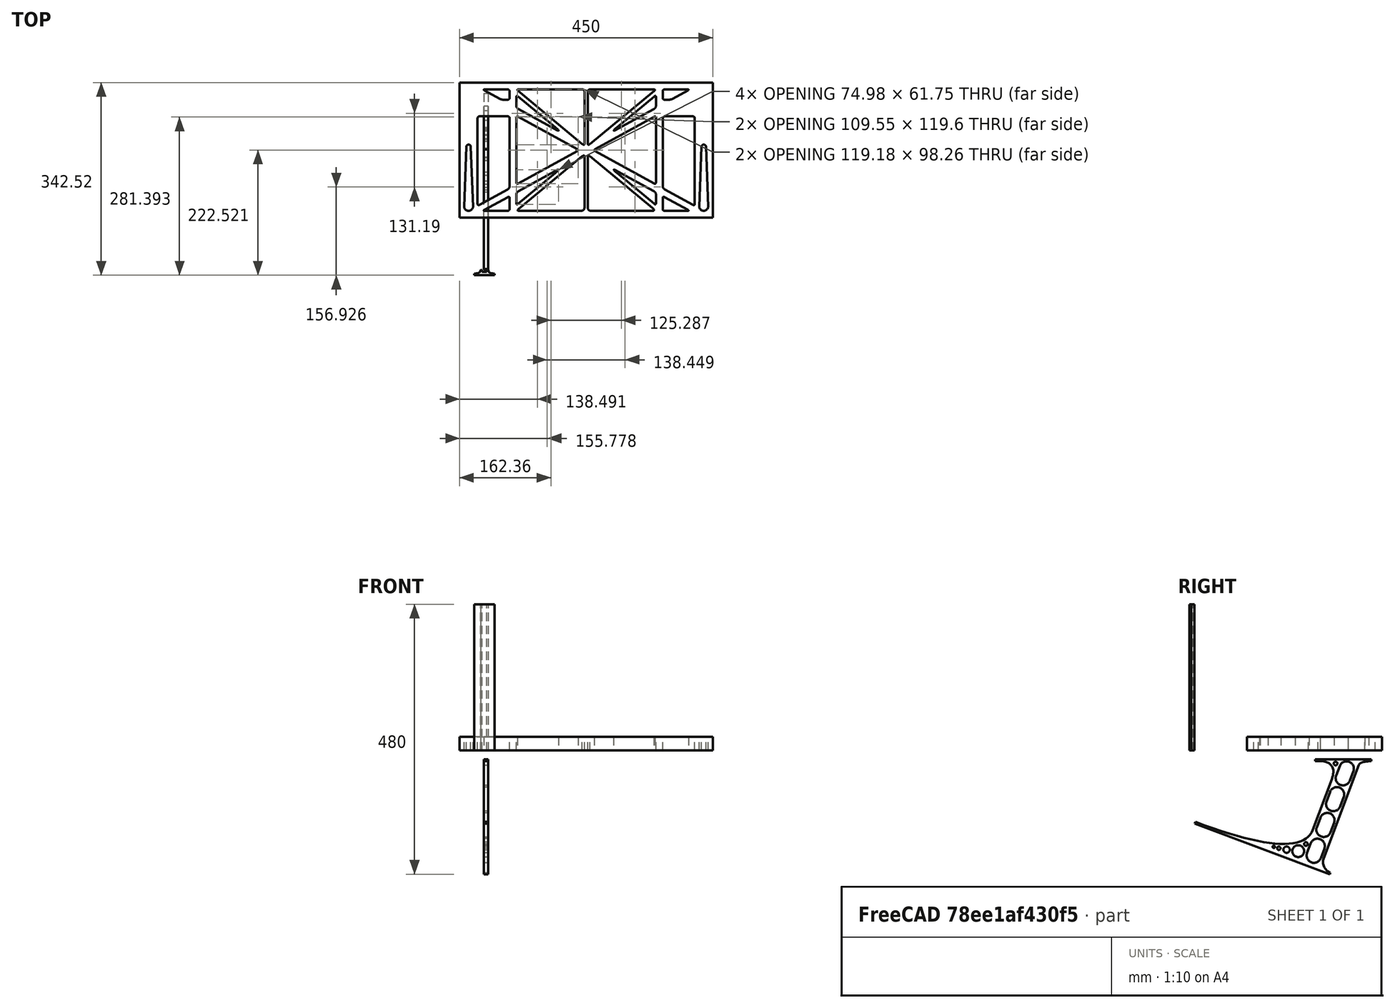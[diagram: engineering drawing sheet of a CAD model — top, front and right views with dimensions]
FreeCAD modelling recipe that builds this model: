
FCSTD DOCUMENT  (FreeCAD 0.19R0.19.2)
Label: laptopStand152FCStd
License: All rights reserved
LicenseURL: http://en.wikipedia.org/wiki/All_rights_reserved
objects: Sketcher::SketchObject×4, Part::Extrusion×3
note: 7 computed .brp shape members not serialized (recipe doc carries the construction recipe); baked Part::Feature solids carry a one-line shape summary decoded from their .brp

FEATURE [Sketcher::SketchObject] Sketch
  FullyConstrained = false
  sketch-geometry (349):
    g0: LineSegment StartX=-10.9272 StartY=-82.7794 StartZ=0 EndX=46.0728 EndY=-51.4823 EndZ=0
    g1: LineSegment StartX=-10.9272 StartY=76.4095 StartZ=0 EndX=-10.9272 EndY=-82.7794 EndZ=0
    g2: LineSegment StartX=46.0728 StartY=76.4095 StartZ=0 EndX=46.0728 EndY=-51.4823 EndZ=0
    g3: LineSegment StartX=-42.9272 StartY=136.221 StartZ=0 EndX=-42.9272 EndY=-103.779 EndZ=0
    g4: LineSegment StartX=407.073 StartY=136.221 StartZ=0 EndX=407.073 EndY=-103.779 EndZ=0
    g5: ArcOfCircle CenterX=-26.9272 CenterY=-83.7794 CenterZ=0 NormalX=0 NormalY=0 NormalZ=1 AngleXU=0 Radius=8 StartAngle=3.14159 EndAngle=6.28319
    g6: ArcOfCircle CenterX=391.073 CenterY=22.1087 CenterZ=0 NormalX=0 NormalY=0 NormalZ=1 AngleXU=0 Radius=8 StartAngle=-4.4e-15 EndAngle=3.14159
    g7: LineSegment StartX=399.073 StartY=22.1087 StartZ=0 EndX=399.073 EndY=-83.7794 EndZ=0
    g8: LineSegment StartX=383.073 StartY=22.1087 StartZ=0 EndX=383.073 EndY=-83.7794 EndZ=0
    g9: ArcOfCircle CenterX=391.073 CenterY=-83.7794 CenterZ=0 NormalX=0 NormalY=0 NormalZ=1 AngleXU=0 Radius=8 StartAngle=3.14159 EndAngle=6.28319
    g10: Circle CenterX=175.022 CenterY=27.0628 CenterZ=0 NormalX=0 NormalY=0 NormalZ=1 AngleXU=0 Radius=1
    g11: Circle CenterX=179.022 CenterY=24.8665 CenterZ=0 NormalX=0 NormalY=0 NormalZ=1 AngleXU=0 Radius=1
    g12: Circle CenterX=179.022 CenterY=27.0628 CenterZ=0 NormalX=0 NormalY=0 NormalZ=1 AngleXU=0 Radius=1
    g13: BSplineCurve PolesCount=3 KnotsCount=2 Degree=2 IsPeriodic=0
    g14: GeomPoint X=175.022 Y=27.0628 Z=0
    g15: GeomPoint X=179.022 Y=27.0628 Z=0
    g16: Circle CenterX=189.124 CenterY=27.0628 CenterZ=0 NormalX=0 NormalY=0 NormalZ=1 AngleXU=0 Radius=1
    g17: Circle CenterX=185.124 CenterY=24.8665 CenterZ=0 NormalX=0 NormalY=0 NormalZ=1 AngleXU=0 Radius=1
    g18: Circle CenterX=185.124 CenterY=27.0628 CenterZ=0 NormalX=0 NormalY=0 NormalZ=1 AngleXU=0 Radius=1
    g19: BSplineCurve PolesCount=3 KnotsCount=2 Degree=2 IsPeriodic=0
    g20: GeomPoint X=189.124 Y=27.0628 Z=0
    g21: GeomPoint X=185.124 Y=27.0628 Z=0
    g22: Circle CenterX=175.022 CenterY=5.37834 CenterZ=0 NormalX=0 NormalY=0 NormalZ=1 AngleXU=0 Radius=1
    g23: Circle CenterX=179.022 CenterY=7.57463 CenterZ=0 NormalX=0 NormalY=0 NormalZ=1 AngleXU=0 Radius=1
    g24: Circle CenterX=179.022 CenterY=5.34704 CenterZ=0 NormalX=0 NormalY=0 NormalZ=1 AngleXU=0 Radius=1
    g25: BSplineCurve PolesCount=3 KnotsCount=2 Degree=2 IsPeriodic=0
    g26: GeomPoint X=175.022 Y=5.37834 Z=0
    g27: GeomPoint X=179.022 Y=5.34704 Z=0
    g28: Circle CenterX=189.124 CenterY=5.37834 CenterZ=0 NormalX=0 NormalY=0 NormalZ=1 AngleXU=0 Radius=1
    g29: Circle CenterX=185.124 CenterY=7.57463 CenterZ=0 NormalX=0 NormalY=0 NormalZ=1 AngleXU=0 Radius=1
    g30: Circle CenterX=185.124 CenterY=5.34704 CenterZ=0 NormalX=0 NormalY=0 NormalZ=1 AngleXU=0 Radius=1
    g31: BSplineCurve PolesCount=3 KnotsCount=2 Degree=2 IsPeriodic=0
    g32: GeomPoint X=189.124 Y=5.37834 Z=0
    g33: GeomPoint X=185.124 Y=5.34704 Z=0
    g34: Circle CenterX=165.871 CenterY=18.1458 CenterZ=0 NormalX=0 NormalY=0 NormalZ=1 AngleXU=0 Radius=1
    g35: Circle CenterX=169.377 CenterY=16.2206 CenterZ=0 NormalX=0 NormalY=0 NormalZ=1 AngleXU=0 Radius=1
    g36: Circle CenterX=165.871 CenterY=14.2954 CenterZ=0 NormalX=0 NormalY=0 NormalZ=1 AngleXU=0 Radius=1
    g37: BSplineCurve PolesCount=3 KnotsCount=2 Degree=2 IsPeriodic=0
    g38: GeomPoint X=165.871 Y=18.1458 Z=0
    g39: GeomPoint X=165.871 Y=14.2954 Z=0
    g40: Circle CenterX=198.275 CenterY=18.1458 CenterZ=0 NormalX=0 NormalY=0 NormalZ=1 AngleXU=0 Radius=1
    g41: Circle CenterX=194.768 CenterY=16.2206 CenterZ=0 NormalX=0 NormalY=0 NormalZ=1 AngleXU=0 Radius=1
    g42: Circle CenterX=198.275 CenterY=14.2954 CenterZ=0 NormalX=0 NormalY=0 NormalZ=1 AngleXU=0 Radius=1
    g43: BSplineCurve PolesCount=3 KnotsCount=2 Degree=2 IsPeriodic=0
    g44: GeomPoint X=198.275 Y=18.1458 Z=0
    g45: GeomPoint X=198.275 Y=14.2954 Z=0
    g46: LineSegment StartX=407.073 StartY=-103.779 StartZ=0 EndX=-42.9272 EndY=-103.779 EndZ=0
    g47: LineSegment StartX=407.073 StartY=136.221 StartZ=0 EndX=-42.9272 EndY=136.221 EndZ=0
    g48: LineSegment StartX=46.0728 StartY=76.4095 StartZ=0 EndX=-10.9272 EndY=76.4095 EndZ=0
    g49: Circle CenterX=125.607 CenterY=54.1951 CenterZ=0 NormalX=0 NormalY=0 NormalZ=1 AngleXU=0 Radius=1
    g50: Circle CenterX=139.632 CenterY=46.4944 CenterZ=0 NormalX=0 NormalY=0 NormalZ=1 AngleXU=0 Radius=1
    g51: Circle CenterX=127.326 CenterY=56.7187 CenterZ=0 NormalX=0 NormalY=0 NormalZ=1 AngleXU=0 Radius=1
    g52: BSplineCurve PolesCount=3 KnotsCount=2 Degree=2 IsPeriodic=0
    g53: GeomPoint X=125.607 Y=54.1951 Z=0
    g54: GeomPoint X=127.326 Y=56.7187 Z=0
    g55: Circle CenterX=236.821 CenterY=56.7187 CenterZ=0 NormalX=0 NormalY=0 NormalZ=1 AngleXU=0 Radius=1
    g56: Circle CenterX=224.513 CenterY=46.4944 CenterZ=0 NormalX=0 NormalY=0 NormalZ=1 AngleXU=0 Radius=1
    g57: Circle CenterX=238.538 CenterY=54.1951 CenterZ=0 NormalX=0 NormalY=0 NormalZ=1 AngleXU=0 Radius=1
    g58: BSplineCurve PolesCount=3 KnotsCount=2 Degree=2 IsPeriodic=0
    g59: GeomPoint X=236.821 Y=56.7187 Z=0
    g60: GeomPoint X=238.538 Y=54.1951 Z=0
    g61: Circle CenterX=238.538 CenterY=-21.7539 CenterZ=0 NormalX=0 NormalY=0 NormalZ=1 AngleXU=0 Radius=1
    g62: Circle CenterX=224.513 CenterY=-14.0532 CenterZ=0 NormalX=0 NormalY=0 NormalZ=1 AngleXU=0 Radius=1
    g63: Circle CenterX=236.821 CenterY=-24.2775 CenterZ=0 NormalX=0 NormalY=0 NormalZ=1 AngleXU=0 Radius=1
    g64: BSplineCurve PolesCount=3 KnotsCount=2 Degree=2 IsPeriodic=0
    g65: GeomPoint X=238.538 Y=-21.7539 Z=0
    g66: GeomPoint X=236.821 Y=-24.2775 Z=0
    g67: Circle CenterX=125.607 CenterY=-21.7539 CenterZ=0 NormalX=0 NormalY=0 NormalZ=1 AngleXU=0 Radius=1
    g68: Circle CenterX=139.632 CenterY=-14.0532 CenterZ=0 NormalX=0 NormalY=0 NormalZ=1 AngleXU=0 Radius=1
    g69: Circle CenterX=127.325 CenterY=-24.2775 CenterZ=0 NormalX=0 NormalY=0 NormalZ=1 AngleXU=0 Radius=1
    g70: BSplineCurve PolesCount=3 KnotsCount=2 Degree=2 IsPeriodic=0
    g71: GeomPoint X=125.607 Y=-21.7539 Z=0
    g72: GeomPoint X=127.325 Y=-24.2775 Z=0
    g73: Circle CenterX=302.996 CenterY=111.695 CenterZ=0 NormalX=0 NormalY=0 NormalZ=1 AngleXU=0 Radius=1
    g74: Circle CenterX=306.073 CenterY=114.251 CenterZ=0 NormalX=0 NormalY=0 NormalZ=1 AngleXU=0 Radius=1
    g75: Circle CenterX=306.073 CenterY=110.251 CenterZ=0 NormalX=0 NormalY=0 NormalZ=1 AngleXU=0 Radius=1
    g76: BSplineCurve PolesCount=3 KnotsCount=2 Degree=2 IsPeriodic=0
    g77: GeomPoint X=302.996 Y=111.695 Z=0
    g78: GeomPoint X=306.073 Y=110.251 Z=0
    g79: Circle CenterX=306.073 CenterY=95.2763 CenterZ=0 NormalX=0 NormalY=0 NormalZ=1 AngleXU=0 Radius=1
    g80: Circle CenterX=306.073 CenterY=91.2763 CenterZ=0 NormalX=0 NormalY=0 NormalZ=1 AngleXU=0 Radius=1
    g81: Circle CenterX=302.567 CenterY=89.3511 CenterZ=0 NormalX=0 NormalY=0 NormalZ=1 AngleXU=0 Radius=1
    g82: BSplineCurve PolesCount=3 KnotsCount=2 Degree=2 IsPeriodic=0
    g83: GeomPoint X=306.073 Y=95.2763 Z=0
    g84: GeomPoint X=302.567 Y=89.3511 Z=0
    g85: LineSegment StartX=306.073 StartY=110.251 StartZ=0 EndX=306.073 EndY=95.2763 EndZ=0
    g86: LineSegment StartX=302.996 StartY=111.695 StartZ=0 EndX=236.821 EndY=56.7187 EndZ=0
    g87: LineSegment StartX=238.538 StartY=54.1951 StartZ=0 EndX=302.567 EndY=89.3511 EndZ=0
    g88: Circle CenterX=61.1496 CenterY=111.695 CenterZ=0 NormalX=0 NormalY=0 NormalZ=1 AngleXU=0 Radius=1
    g89: Circle CenterX=58.0728 CenterY=114.251 CenterZ=0 NormalX=0 NormalY=0 NormalZ=1 AngleXU=0 Radius=1
    g90: Circle CenterX=58.0728 CenterY=110.251 CenterZ=0 NormalX=0 NormalY=0 NormalZ=1 AngleXU=0 Radius=1
    g91: BSplineCurve PolesCount=3 KnotsCount=2 Degree=2 IsPeriodic=0
    g92: GeomPoint X=61.1496 Y=111.695 Z=0
    g93: GeomPoint X=58.0728 Y=110.251 Z=0
    g94: Circle CenterX=61.5791 CenterY=89.3511 CenterZ=0 NormalX=0 NormalY=0 NormalZ=1 AngleXU=0 Radius=1
    g95: Circle CenterX=58.0728 CenterY=91.2763 CenterZ=0 NormalX=0 NormalY=0 NormalZ=1 AngleXU=0 Radius=1
    g96: Circle CenterX=58.0728 CenterY=95.2763 CenterZ=0 NormalX=0 NormalY=0 NormalZ=1 AngleXU=0 Radius=1
    g97: BSplineCurve PolesCount=3 KnotsCount=2 Degree=2 IsPeriodic=0
    g98: GeomPoint X=61.5791 Y=89.3511 Z=0
    g99: GeomPoint X=58.0728 Y=95.2763 Z=0
    g100: LineSegment StartX=58.0728 StartY=110.251 StartZ=0 EndX=58.0728 EndY=95.2763 EndZ=0
    g101: LineSegment StartX=61.1496 StartY=111.695 StartZ=0 EndX=127.326 EndY=56.7187 EndZ=0
    g102: LineSegment StartX=125.607 StartY=54.1951 StartZ=0 EndX=61.5791 EndY=89.3511 EndZ=0
    g103: Circle CenterX=61.5791 CenterY=-56.9099 CenterZ=0 NormalX=0 NormalY=0 NormalZ=1 AngleXU=0 Radius=1
    g104: Circle CenterX=58.0728 CenterY=-58.8351 CenterZ=0 NormalX=0 NormalY=0 NormalZ=1 AngleXU=0 Radius=1
    g105: Circle CenterX=58.0728 CenterY=-62.8351 CenterZ=0 NormalX=0 NormalY=0 NormalZ=1 AngleXU=0 Radius=1
    g106: BSplineCurve PolesCount=3 KnotsCount=2 Degree=2 IsPeriodic=0
    g107: GeomPoint X=61.5791 Y=-56.9099 Z=0
    g108: GeomPoint X=58.0728 Y=-62.8351 Z=0
    g109: Circle CenterX=58.0728 CenterY=-77.8102 CenterZ=0 NormalX=0 NormalY=0 NormalZ=1 AngleXU=0 Radius=1
    g110: Circle CenterX=58.0728 CenterY=-81.8102 CenterZ=0 NormalX=0 NormalY=0 NormalZ=1 AngleXU=0 Radius=1
    g111: Circle CenterX=61.1496 CenterY=-79.2541 CenterZ=0 NormalX=0 NormalY=0 NormalZ=1 AngleXU=0 Radius=1
    g112: BSplineCurve PolesCount=3 KnotsCount=2 Degree=2 IsPeriodic=0
    g113: GeomPoint X=58.0728 Y=-77.8102 Z=0
    g114: GeomPoint X=61.1496 Y=-79.2541 Z=0
    g115: LineSegment StartX=58.0728 StartY=-62.8351 StartZ=0 EndX=58.0728 EndY=-77.8102 EndZ=0
    g116: LineSegment StartX=61.1496 StartY=-79.2541 StartZ=0 EndX=127.325 EndY=-24.2775 EndZ=0
    g117: LineSegment StartX=125.607 StartY=-21.7539 StartZ=0 EndX=61.5791 EndY=-56.9099 EndZ=0
    g118: Circle CenterX=302.567 CenterY=-56.9099 CenterZ=0 NormalX=0 NormalY=0 NormalZ=1 AngleXU=0 Radius=1
    g119: Circle CenterX=306.073 CenterY=-58.8351 CenterZ=0 NormalX=0 NormalY=0 NormalZ=1 AngleXU=0 Radius=1
    g120: Circle CenterX=306.073 CenterY=-62.8351 CenterZ=0 NormalX=0 NormalY=0 NormalZ=1 AngleXU=0 Radius=1
    g121: BSplineCurve PolesCount=3 KnotsCount=2 Degree=2 IsPeriodic=0
    g122: GeomPoint X=302.567 Y=-56.9099 Z=0
    g123: GeomPoint X=306.073 Y=-62.8351 Z=0
    g124: Circle CenterX=302.996 CenterY=-79.2541 CenterZ=0 NormalX=0 NormalY=0 NormalZ=1 AngleXU=0 Radius=1
    g125: Circle CenterX=306.073 CenterY=-81.8102 CenterZ=0 NormalX=0 NormalY=0 NormalZ=1 AngleXU=0 Radius=1
    g126: Circle CenterX=306.073 CenterY=-77.8102 CenterZ=0 NormalX=0 NormalY=0 NormalZ=1 AngleXU=0 Radius=1
    g127: BSplineCurve PolesCount=3 KnotsCount=2 Degree=2 IsPeriodic=0
    g128: GeomPoint X=302.996 Y=-79.2541 Z=0
    g129: GeomPoint X=306.073 Y=-77.8102 Z=0
    g130: LineSegment StartX=306.073 StartY=-62.8351 StartZ=0 EndX=306.073 EndY=-77.8102 EndZ=0
    g131: LineSegment StartX=302.996 StartY=-79.2541 StartZ=0 EndX=236.821 EndY=-24.2775 EndZ=0
    g132: LineSegment StartX=238.538 StartY=-21.7539 StartZ=0 EndX=302.567 EndY=-56.9099 EndZ=0
    g133: Circle CenterX=61.6457 CenterY=-88.8112 CenterZ=0 NormalX=0 NormalY=0 NormalZ=1 AngleXU=0 Radius=1
    g134: Circle CenterX=58.0728 CenterY=-91.7794 CenterZ=0 NormalX=0 NormalY=0 NormalZ=1 AngleXU=0 Radius=1
    g135: Circle CenterX=63.9135 CenterY=-91.7794 CenterZ=0 NormalX=0 NormalY=0 NormalZ=1 AngleXU=0 Radius=1
    g136: BSplineCurve PolesCount=3 KnotsCount=2 Degree=2 IsPeriodic=0
    g137: GeomPoint X=61.6457 Y=-88.8112 Z=0
    g138: GeomPoint X=63.9135 Y=-91.7794 Z=0
    g139: Circle CenterX=179.022 CenterY=-85.8163 CenterZ=0 NormalX=0 NormalY=0 NormalZ=1 AngleXU=0 Radius=1
    g140: Circle CenterX=179.022 CenterY=-91.7794 CenterZ=0 NormalX=0 NormalY=0 NormalZ=1 AngleXU=0 Radius=1
    g141: Circle CenterX=171.895 CenterY=-91.7794 CenterZ=0 NormalX=0 NormalY=0 NormalZ=1 AngleXU=0 Radius=1
    g142: BSplineCurve PolesCount=3 KnotsCount=2 Degree=2 IsPeriodic=0
    g143: GeomPoint X=179.022 Y=-85.8163 Z=0
    g144: GeomPoint X=171.895 Y=-91.7794 Z=0
    g145: Circle CenterX=185.124 CenterY=-86.2028 CenterZ=0 NormalX=0 NormalY=0 NormalZ=1 AngleXU=0 Radius=1
    g146: Circle CenterX=185.124 CenterY=-91.7794 CenterZ=0 NormalX=0 NormalY=0 NormalZ=1 AngleXU=0 Radius=1
    g147: Circle CenterX=191.747 CenterY=-91.7794 CenterZ=0 NormalX=0 NormalY=0 NormalZ=1 AngleXU=0 Radius=1
    g148: BSplineCurve PolesCount=3 KnotsCount=2 Degree=2 IsPeriodic=0
    g149: GeomPoint X=185.124 Y=-86.2028 Z=0
    g150: GeomPoint X=191.747 Y=-91.7794 Z=0
    g151: Circle CenterX=299.888 CenterY=-86.6413 CenterZ=0 NormalX=0 NormalY=0 NormalZ=1 AngleXU=0 Radius=1
    g152: Circle CenterX=306.073 CenterY=-91.7794 CenterZ=0 NormalX=0 NormalY=0 NormalZ=1 AngleXU=0 Radius=1
    g153: Circle CenterX=298.776 CenterY=-91.7794 CenterZ=0 NormalX=0 NormalY=0 NormalZ=1 AngleXU=0 Radius=1
    g154: BSplineCurve PolesCount=3 KnotsCount=2 Degree=2 IsPeriodic=0
    g155: GeomPoint X=299.888 Y=-86.6413 Z=0
    g156: GeomPoint X=298.776 Y=-91.7794 Z=0
    g157: LineSegment StartX=189.124 StartY=5.37834 StartZ=0 EndX=299.888 EndY=-86.6413 EndZ=0
    g158: LineSegment StartX=298.776 StartY=-91.7794 StartZ=0 EndX=191.747 EndY=-91.7794 EndZ=0
    g159: LineSegment StartX=185.124 StartY=-86.2028 StartZ=0 EndX=185.124 EndY=5.34704 EndZ=0
    g160: LineSegment StartX=179.022 StartY=5.34704 StartZ=0 EndX=179.022 EndY=-85.8163 EndZ=0
    g161: LineSegment StartX=171.895 StartY=-91.7794 StartZ=0 EndX=63.9135 EndY=-91.7794 EndZ=0
    g162: LineSegment StartX=61.6457 StartY=-88.8112 StartZ=0 EndX=175.022 EndY=5.37834 EndZ=0
    g163: Circle CenterX=302.073 CenterY=124.221 CenterZ=0 NormalX=0 NormalY=0 NormalZ=1 AngleXU=0 Radius=1
    g164: Circle CenterX=306.073 CenterY=124.221 CenterZ=0 NormalX=0 NormalY=0 NormalZ=1 AngleXU=0 Radius=1
    g165: Circle CenterX=302.996 CenterY=121.665 CenterZ=0 NormalX=0 NormalY=0 NormalZ=1 AngleXU=0 Radius=1
    g166: BSplineCurve PolesCount=3 KnotsCount=2 Degree=2 IsPeriodic=0
    g167: GeomPoint X=302.073 Y=124.221 Z=0
    g168: GeomPoint X=302.996 Y=121.665 Z=0
    g169: Circle CenterX=189.124 CenterY=124.221 CenterZ=0 NormalX=0 NormalY=0 NormalZ=1 AngleXU=0 Radius=1
    g170: Circle CenterX=185.124 CenterY=124.221 CenterZ=0 NormalX=0 NormalY=0 NormalZ=1 AngleXU=0 Radius=1
    g171: Circle CenterX=185.124 CenterY=120.221 CenterZ=0 NormalX=0 NormalY=0 NormalZ=1 AngleXU=0 Radius=1
    g172: BSplineCurve PolesCount=3 KnotsCount=2 Degree=2 IsPeriodic=0
    g173: GeomPoint X=189.124 Y=124.221 Z=0
    g174: GeomPoint X=185.124 Y=120.221 Z=0
    g175: Circle CenterX=175.022 CenterY=124.221 CenterZ=0 NormalX=0 NormalY=0 NormalZ=1 AngleXU=0 Radius=1
    g176: Circle CenterX=179.022 CenterY=124.221 CenterZ=0 NormalX=0 NormalY=0 NormalZ=1 AngleXU=0 Radius=1
    g177: Circle CenterX=179.022 CenterY=120.221 CenterZ=0 NormalX=0 NormalY=0 NormalZ=1 AngleXU=0 Radius=1
    g178: BSplineCurve PolesCount=3 KnotsCount=2 Degree=2 IsPeriodic=0
    g179: GeomPoint X=175.022 Y=124.221 Z=0
    g180: GeomPoint X=179.022 Y=120.221 Z=0
    g181: Circle CenterX=62.0728 CenterY=124.221 CenterZ=0 NormalX=0 NormalY=0 NormalZ=1 AngleXU=0 Radius=1
    g182: Circle CenterX=58.0728 CenterY=124.221 CenterZ=0 NormalX=0 NormalY=0 NormalZ=1 AngleXU=0 Radius=1
    g183: Circle CenterX=61.1496 CenterY=121.665 CenterZ=0 NormalX=0 NormalY=0 NormalZ=1 AngleXU=0 Radius=1
    g184: BSplineCurve PolesCount=3 KnotsCount=2 Degree=2 IsPeriodic=0
    g185: GeomPoint X=62.0728 Y=124.221 Z=0
    g186: GeomPoint X=61.1496 Y=121.665 Z=0
    g187: LineSegment StartX=62.0728 StartY=124.221 StartZ=0 EndX=175.022 EndY=124.221 EndZ=0
    g188: LineSegment StartX=179.022 StartY=120.221 StartZ=0 EndX=179.022 EndY=27.0628 EndZ=0
    g189: LineSegment StartX=185.124 StartY=27.0628 StartZ=0 EndX=185.124 EndY=120.221 EndZ=0
    g190: LineSegment StartX=189.124 StartY=124.221 StartZ=0 EndX=302.073 EndY=124.221 EndZ=0
    g191: LineSegment StartX=302.996 StartY=121.665 StartZ=0 EndX=189.124 EndY=27.0628 EndZ=0
    g192: LineSegment StartX=175.022 StartY=27.0628 StartZ=0 EndX=61.1496 EndY=121.665 EndZ=0
    g193: Circle CenterX=61.5791 CenterY=75.4095 CenterZ=0 NormalX=0 NormalY=0 NormalZ=1 AngleXU=0 Radius=1
    g194: Circle CenterX=58.0728 CenterY=77.3346 CenterZ=0 NormalX=0 NormalY=0 NormalZ=1 AngleXU=0 Radius=1
    g195: Circle CenterX=58.0728 CenterY=73.3346 CenterZ=0 NormalX=0 NormalY=0 NormalZ=1 AngleXU=0 Radius=1
    g196: BSplineCurve PolesCount=3 KnotsCount=2 Degree=2 IsPeriodic=0
    g197: GeomPoint X=61.5791 Y=75.4095 Z=0
    g198: GeomPoint X=58.0728 Y=73.3346 Z=0
    g199: Circle CenterX=58.0728 CenterY=-40.8935 CenterZ=0 NormalX=0 NormalY=0 NormalZ=1 AngleXU=0 Radius=1
    g200: Circle CenterX=58.0728 CenterY=-44.8935 CenterZ=0 NormalX=0 NormalY=0 NormalZ=1 AngleXU=0 Radius=1
    g201: Circle CenterX=61.5791 CenterY=-42.9683 CenterZ=0 NormalX=0 NormalY=0 NormalZ=1 AngleXU=0 Radius=1
    g202: BSplineCurve PolesCount=3 KnotsCount=2 Degree=2 IsPeriodic=0
    g203: GeomPoint X=58.0728 Y=-40.8935 Z=0
    g204: GeomPoint X=61.5791 Y=-42.9683 Z=0
    g205: LineSegment StartX=61.5791 StartY=-42.9683 StartZ=0 EndX=165.871 EndY=14.2954 EndZ=0
    g206: LineSegment StartX=165.871 StartY=18.1458 StartZ=0 EndX=61.5791 EndY=75.4095 EndZ=0
    g207: LineSegment StartX=58.0728 StartY=73.3346 StartZ=0 EndX=58.0728 EndY=-40.8935 EndZ=0
    g208: Circle CenterX=302.567 CenterY=-42.9683 CenterZ=0 NormalX=0 NormalY=0 NormalZ=1 AngleXU=0 Radius=1
    g209: Circle CenterX=306.073 CenterY=-44.8935 CenterZ=0 NormalX=0 NormalY=0 NormalZ=1 AngleXU=0 Radius=1
    g210: Circle CenterX=306.073 CenterY=-40.8935 CenterZ=0 NormalX=0 NormalY=0 NormalZ=1 AngleXU=0 Radius=1
    g211: BSplineCurve PolesCount=3 KnotsCount=2 Degree=2 IsPeriodic=0
    g212: GeomPoint X=302.567 Y=-42.9683 Z=0
    g213: GeomPoint X=306.073 Y=-40.8935 Z=0
    g214: Circle CenterX=306.073 CenterY=73.3346 CenterZ=0 NormalX=0 NormalY=0 NormalZ=1 AngleXU=0 Radius=1
    g215: Circle CenterX=306.073 CenterY=77.3346 CenterZ=0 NormalX=0 NormalY=0 NormalZ=1 AngleXU=0 Radius=1
    g216: Circle CenterX=302.567 CenterY=75.4095 CenterZ=0 NormalX=0 NormalY=0 NormalZ=1 AngleXU=0 Radius=1
    g217: BSplineCurve PolesCount=3 KnotsCount=2 Degree=2 IsPeriodic=0
    g218: GeomPoint X=306.073 Y=73.3346 Z=0
    g219: GeomPoint X=302.567 Y=75.4095 Z=0
    g220: LineSegment StartX=302.567 StartY=-42.9683 StartZ=0 EndX=198.275 EndY=14.2954 EndZ=0
    g221: LineSegment StartX=198.275 StartY=18.1458 StartZ=0 EndX=302.567 EndY=75.4095 EndZ=0
    g222: LineSegment StartX=306.073 StartY=73.3346 StartZ=0 EndX=306.073 EndY=-40.8935 EndZ=0
    g223: LineSegment StartX=322.073 StartY=105.865 StartZ=0 EndX=328.643 EndY=105.865 EndZ=0
    g224: LineSegment StartX=318.073 StartY=120.221 StartZ=0 EndX=318.073 EndY=109.865 EndZ=0
    g225: LineSegment StartX=336.157 StartY=107.779 StartZ=0 EndX=362.567 EndY=122.294 EndZ=0
    g226: Circle CenterX=362.073 CenterY=124.221 CenterZ=0 NormalX=0 NormalY=0 NormalZ=1 AngleXU=0 Radius=1
    g227: Circle CenterX=366.073 CenterY=124.221 CenterZ=0 NormalX=0 NormalY=0 NormalZ=1 AngleXU=0 Radius=1
    g228: Circle CenterX=362.567 CenterY=122.294 CenterZ=0 NormalX=0 NormalY=0 NormalZ=1 AngleXU=0 Radius=1
    g229: BSplineCurve PolesCount=3 KnotsCount=2 Degree=2 IsPeriodic=0
    g230: GeomPoint X=362.073 Y=124.221 Z=0
    g231: GeomPoint X=362.567 Y=122.294 Z=0
    g232: Circle CenterX=322.073 CenterY=124.221 CenterZ=0 NormalX=0 NormalY=0 NormalZ=1 AngleXU=0 Radius=1
    g233: Circle CenterX=318.073 CenterY=124.221 CenterZ=0 NormalX=0 NormalY=0 NormalZ=1 AngleXU=0 Radius=1
    g234: Circle CenterX=318.073 CenterY=120.221 CenterZ=0 NormalX=0 NormalY=0 NormalZ=1 AngleXU=0 Radius=1
    g235: BSplineCurve PolesCount=3 KnotsCount=2 Degree=2 IsPeriodic=0
    g236: GeomPoint X=322.073 Y=124.221 Z=0
    g237: GeomPoint X=318.073 Y=120.221 Z=0
    g238: Circle CenterX=322.073 CenterY=105.865 CenterZ=0 NormalX=0 NormalY=0 NormalZ=1 AngleXU=0 Radius=1
    g239: Circle CenterX=318.073 CenterY=105.865 CenterZ=0 NormalX=0 NormalY=0 NormalZ=1 AngleXU=0 Radius=1
    g240: Circle CenterX=318.073 CenterY=109.865 CenterZ=0 NormalX=0 NormalY=0 NormalZ=1 AngleXU=0 Radius=1
    g241: BSplineCurve PolesCount=3 KnotsCount=2 Degree=2 IsPeriodic=0
    g242: GeomPoint X=322.073 Y=105.865 Z=0
    g243: GeomPoint X=318.073 Y=109.865 Z=0
    g244: Circle CenterX=336.157 CenterY=107.779 CenterZ=0 NormalX=0 NormalY=0 NormalZ=1 AngleXU=0 Radius=1
    g245: Circle CenterX=332.651 CenterY=105.853 CenterZ=0 NormalX=0 NormalY=0 NormalZ=1 AngleXU=0 Radius=1
    g246: Circle CenterX=328.643 CenterY=105.865 CenterZ=0 NormalX=0 NormalY=0 NormalZ=1 AngleXU=0 Radius=1
    g247: BSplineCurve PolesCount=3 KnotsCount=2 Degree=2 IsPeriodic=0
    g248: GeomPoint X=336.157 Y=107.779 Z=0
    g249: GeomPoint X=328.643 Y=105.865 Z=0
    g250: LineSegment StartX=322.073 StartY=124.221 StartZ=0 EndX=362.073 EndY=124.221 EndZ=0
    g251: Circle CenterX=371.567 CenterY=-80.8644 CenterZ=0 NormalX=0 NormalY=0 NormalZ=1 AngleXU=0 Radius=1
    g252: Circle CenterX=375.073 CenterY=-82.7896 CenterZ=0 NormalX=0 NormalY=0 NormalZ=1 AngleXU=0 Radius=1
    g253: Circle CenterX=375.073 CenterY=-78.7896 CenterZ=0 NormalX=0 NormalY=0 NormalZ=1 AngleXU=0 Radius=1
    g254: BSplineCurve PolesCount=3 KnotsCount=2 Degree=2 IsPeriodic=0
    g255: GeomPoint X=371.567 Y=-80.8644 Z=0
    g256: GeomPoint X=375.073 Y=-78.7896 Z=0
    g257: Circle CenterX=321.579 CenterY=-53.4075 CenterZ=0 NormalX=0 NormalY=0 NormalZ=1 AngleXU=0 Radius=1
    g258: Circle CenterX=318.073 CenterY=-51.4823 CenterZ=0 NormalX=0 NormalY=0 NormalZ=1 AngleXU=0 Radius=1
    g259: Circle CenterX=318.073 CenterY=-47.4805 CenterZ=0 NormalX=0 NormalY=0 NormalZ=1 AngleXU=0 Radius=1
    g260: BSplineCurve PolesCount=3 KnotsCount=2 Degree=2 IsPeriodic=0
    g261: GeomPoint X=321.579 Y=-53.4075 Z=0
    g262: GeomPoint X=318.073 Y=-47.4805 Z=0
    g263: LineSegment StartX=371.567 StartY=-80.8644 StartZ=0 EndX=321.579 EndY=-53.4075 EndZ=0
    g264: Circle CenterX=321.579 CenterY=-67.3492 CenterZ=0 NormalX=0 NormalY=0 NormalZ=1 AngleXU=0 Radius=1
    g265: Circle CenterX=318.073 CenterY=-65.424 CenterZ=0 NormalX=0 NormalY=0 NormalZ=1 AngleXU=0 Radius=1
    g266: Circle CenterX=318.073 CenterY=-69.424 CenterZ=0 NormalX=0 NormalY=0 NormalZ=1 AngleXU=0 Radius=1
    g267: BSplineCurve PolesCount=3 KnotsCount=2 Degree=2 IsPeriodic=0
    g268: GeomPoint X=321.579 Y=-67.3492 Z=0
    g269: GeomPoint X=318.073 Y=-69.424 Z=0
    g270: Circle CenterX=362.567 CenterY=-89.8542 CenterZ=0 NormalX=0 NormalY=0 NormalZ=1 AngleXU=0 Radius=1
    g271: Circle CenterX=366.073 CenterY=-91.7794 CenterZ=0 NormalX=0 NormalY=0 NormalZ=1 AngleXU=0 Radius=1
    g272: Circle CenterX=362.073 CenterY=-91.7794 CenterZ=0 NormalX=0 NormalY=0 NormalZ=1 AngleXU=0 Radius=1
    g273: BSplineCurve PolesCount=3 KnotsCount=2 Degree=2 IsPeriodic=0
    g274: GeomPoint X=362.567 Y=-89.8542 Z=0
    g275: GeomPoint X=362.073 Y=-91.7794 Z=0
    g276: Circle CenterX=322.073 CenterY=-91.7794 CenterZ=0 NormalX=0 NormalY=0 NormalZ=1 AngleXU=0 Radius=1
    g277: Circle CenterX=318.073 CenterY=-91.7794 CenterZ=0 NormalX=0 NormalY=0 NormalZ=1 AngleXU=0 Radius=1
    g278: Circle CenterX=318.073 CenterY=-87.7794 CenterZ=0 NormalX=0 NormalY=0 NormalZ=1 AngleXU=0 Radius=1
    g279: BSplineCurve PolesCount=3 KnotsCount=2 Degree=2 IsPeriodic=0
    g280: GeomPoint X=322.073 Y=-91.7794 Z=0
    g281: GeomPoint X=318.073 Y=-87.7794 Z=0
    g282: LineSegment StartX=362.567 StartY=-89.8542 StartZ=0 EndX=321.579 EndY=-67.3492 EndZ=0
    g283: LineSegment StartX=318.073 StartY=-69.424 StartZ=0 EndX=318.073 EndY=-87.7794 EndZ=0
    g284: LineSegment StartX=322.073 StartY=-91.7794 StartZ=0 EndX=362.073 EndY=-91.7794 EndZ=0
    g285: Circle CenterX=2.07281 CenterY=124.221 CenterZ=0 NormalX=0 NormalY=0 NormalZ=1 AngleXU=0 Radius=1
    g286: Circle CenterX=1.57905 CenterY=122.295 CenterZ=0 NormalX=0 NormalY=0 NormalZ=1 AngleXU=0 Radius=1
    g287: BSplineCurve PolesCount=3 KnotsCount=2 Degree=2 IsPeriodic=0
    g288: GeomPoint X=2.07281 Y=124.221 Z=0
    g289: GeomPoint X=1.57905 Y=122.295 Z=0
    g290: Circle CenterX=42.0728 CenterY=124.221 CenterZ=0 NormalX=0 NormalY=0 NormalZ=1 AngleXU=0 Radius=1
    g291: Circle CenterX=46.0728 CenterY=124.221 CenterZ=0 NormalX=0 NormalY=0 NormalZ=1 AngleXU=0 Radius=1
    g292: Circle CenterX=46.0728 CenterY=120.221 CenterZ=0 NormalX=0 NormalY=0 NormalZ=1 AngleXU=0 Radius=1
    g293: BSplineCurve PolesCount=3 KnotsCount=2 Degree=2 IsPeriodic=0
    g294: GeomPoint X=42.0728 Y=124.221 Z=0
    g295: GeomPoint X=46.0728 Y=120.221 Z=0
    g296: Circle CenterX=46.0728 CenterY=109.865 CenterZ=0 NormalX=0 NormalY=0 NormalZ=1 AngleXU=0 Radius=1
    g297: Circle CenterX=46.0728 CenterY=105.865 CenterZ=0 NormalX=0 NormalY=0 NormalZ=1 AngleXU=0 Radius=1
    g298: Circle CenterX=42.0728 CenterY=105.865 CenterZ=0 NormalX=0 NormalY=0 NormalZ=1 AngleXU=0 Radius=1
    g299: BSplineCurve PolesCount=3 KnotsCount=2 Degree=2 IsPeriodic=0
    g300: GeomPoint X=46.0728 Y=109.865 Z=0
    g301: GeomPoint X=42.0728 Y=105.865 Z=0
    g302: Circle CenterX=35.5028 CenterY=105.865 CenterZ=0 NormalX=0 NormalY=0 NormalZ=1 AngleXU=0 Radius=1
    g303: Circle CenterX=31.5028 CenterY=105.865 CenterZ=0 NormalX=0 NormalY=0 NormalZ=1 AngleXU=0 Radius=1
    g304: Circle CenterX=27.9965 CenterY=107.79 CenterZ=0 NormalX=0 NormalY=0 NormalZ=1 AngleXU=0 Radius=1
    g305: BSplineCurve PolesCount=3 KnotsCount=2 Degree=2 IsPeriodic=0
    g306: GeomPoint X=35.5028 Y=105.865 Z=0
    g307: GeomPoint X=27.9965 Y=107.79 Z=0
    g308: LineSegment StartX=2.07281 StartY=124.221 StartZ=0 EndX=42.0728 EndY=124.221 EndZ=0
    g309: LineSegment StartX=46.0728 StartY=120.221 StartZ=0 EndX=46.0728 EndY=109.865 EndZ=0
    g310: LineSegment StartX=42.0728 StartY=105.865 StartZ=0 EndX=35.5028 EndY=105.865 EndZ=0
    g311: LineSegment StartX=27.9965 StartY=107.79 StartZ=0 EndX=1.57905 EndY=122.295 EndZ=0
    g312: Circle CenterX=42.5666 CenterY=-67.3492 CenterZ=0 NormalX=0 NormalY=0 NormalZ=1 AngleXU=0 Radius=1
    g313: Circle CenterX=46.0728 CenterY=-65.424 CenterZ=0 NormalX=0 NormalY=0 NormalZ=1 AngleXU=0 Radius=1
    g314: Circle CenterX=46.0728 CenterY=-69.424 CenterZ=0 NormalX=0 NormalY=0 NormalZ=1 AngleXU=0 Radius=1
    g315: BSplineCurve PolesCount=3 KnotsCount=2 Degree=2 IsPeriodic=0
    g316: GeomPoint X=42.5666 Y=-67.3492 Z=0
    g317: GeomPoint X=46.0728 Y=-69.424 Z=0
    g318: Circle CenterX=46.0728 CenterY=-87.7794 CenterZ=0 NormalX=0 NormalY=0 NormalZ=1 AngleXU=0 Radius=1
    g319: Circle CenterX=46.0728 CenterY=-91.7794 CenterZ=0 NormalX=0 NormalY=0 NormalZ=1 AngleXU=0 Radius=1
    g320: Circle CenterX=42.0728 CenterY=-91.7794 CenterZ=0 NormalX=0 NormalY=0 NormalZ=1 AngleXU=0 Radius=1
    g321: BSplineCurve PolesCount=3 KnotsCount=2 Degree=2 IsPeriodic=0
    g322: GeomPoint X=46.0728 Y=-87.7794 Z=0
    g323: GeomPoint X=42.0728 Y=-91.7794 Z=0
    g324: Circle CenterX=2.07281 CenterY=-91.7794 CenterZ=0 NormalX=0 NormalY=0 NormalZ=1 AngleXU=0 Radius=1
    g325: Circle CenterX=-1.92719 CenterY=-91.7794 CenterZ=0 NormalX=0 NormalY=0 NormalZ=1 AngleXU=0 Radius=1
    g326: Circle CenterX=1.57905 CenterY=-89.8542 CenterZ=0 NormalX=0 NormalY=0 NormalZ=1 AngleXU=0 Radius=1
    g327: BSplineCurve PolesCount=3 KnotsCount=2 Degree=2 IsPeriodic=0
    g328: GeomPoint X=2.07281 Y=-91.7794 Z=0
    g329: GeomPoint X=1.57905 Y=-89.8542 Z=0
    g330: LineSegment StartX=2.07281 StartY=-91.7794 StartZ=0 EndX=42.0728 EndY=-91.7794 EndZ=0
    g331: LineSegment StartX=46.0728 StartY=-87.7794 StartZ=0 EndX=46.0728 EndY=-69.424 EndZ=0
    g332: LineSegment StartX=42.5666 StartY=-67.3492 StartZ=0 EndX=1.57905 EndY=-89.8542 EndZ=0
    g333: Circle CenterX=322.073 CenterY=76.4095 CenterZ=0 NormalX=0 NormalY=0 NormalZ=1 AngleXU=0 Radius=4
    g334: BSplineCurve PolesCount=3 KnotsCount=2 Degree=2 IsPeriodic=0
    g335: GeomPoint X=318.073 Y=72.4095 Z=0
    g336: GeomPoint X=322.073 Y=76.4095 Z=0
    g337: Circle CenterX=375.073 CenterY=72.4095 CenterZ=0 NormalX=0 NormalY=0 NormalZ=1 AngleXU=0 Radius=1
    g338: Circle CenterX=375.073 CenterY=76.4095 CenterZ=0 NormalX=0 NormalY=0 NormalZ=1 AngleXU=0 Radius=1
    g339: Circle CenterX=371.073 CenterY=76.4095 CenterZ=0 NormalX=0 NormalY=0 NormalZ=1 AngleXU=0 Radius=1
    g340: BSplineCurve PolesCount=3 KnotsCount=2 Degree=2 IsPeriodic=0
    g341: GeomPoint X=375.073 Y=72.4095 Z=0
    g342: GeomPoint X=371.073 Y=76.4095 Z=0
    g343: LineSegment StartX=322.073 StartY=76.4095 StartZ=0 EndX=371.073 EndY=76.4095 EndZ=0
    g344: LineSegment StartX=318.073 StartY=72.4095 StartZ=0 EndX=318.073 EndY=-47.4805 EndZ=0
    g345: LineSegment StartX=375.073 StartY=72.4095 StartZ=0 EndX=375.073 EndY=-78.7896 EndZ=0
    g346: ArcOfCircle CenterX=-26.9272 CenterY=22.1087 CenterZ=0 NormalX=0 NormalY=0 NormalZ=1 AngleXU=0 Radius=4 StartAngle=5e-16 EndAngle=3.14159
    g347: LineSegment StartX=-30.9272 StartY=22.1087 StartZ=0 EndX=-34.9272 EndY=-83.7794 EndZ=0
    g348: LineSegment StartX=-18.9272 StartY=-83.7794 StartZ=0 EndX=-22.9272 EndY=22.1087 EndZ=0
  constraints (572):
    c: Coincident(g0,g2)
    c: Block(g0)
    c: Block(g1)
    c: Vertical(g3)
    c: Vertical(g4)
    c: Block(g4)
    c: Block(g3)
    c: Tangent(g6,g7) = 1.5708
    c: Tangent(g7,g9) = 1.5708
    c: Equal(g6,g9)
    c: Coincident(g8,g6)
    c: Coincident(g8,g9)
    c: Block(g7)
    c: Block(g8)
    c: Weight(g10) = 1
    c: Equal(g10,g11)
    c: Equal(g10,g12)
    c: InternalAlignment(g10,g13)
    c: InternalAlignment(g11,g13)
    c: InternalAlignment(g12,g13)
    c: InternalAlignment(g14,g13)
    c: InternalAlignment(g15,g13)
    c: Weight(g16) = 1
    c: Equal(g16,g17)
    c: Equal(g16,g18)
    c: InternalAlignment(g16,g19)
    c: InternalAlignment(g17,g19)
    c: InternalAlignment(g18,g19)
    c: InternalAlignment(g20,g19)
    c: InternalAlignment(g21,g19)
    c: Block(g19)
    c: Block(g13)
    c: Weight(g22) = 1
    c: Equal(g22,g23)
    c: Equal(g22,g24)
    c: InternalAlignment(g22,g25)
    c: InternalAlignment(g23,g25)
    c: InternalAlignment(g24,g25)
    c: InternalAlignment(g26,g25)
    c: InternalAlignment(g27,g25)
    c: Weight(g28) = 1
    c: Equal(g28,g29)
    c: Equal(g28,g30)
    c: InternalAlignment(g28,g31)
    c: InternalAlignment(g29,g31)
    c: InternalAlignment(g30,g31)
    c: InternalAlignment(g32,g31)
    c: InternalAlignment(g33,g31)
    c: Block(g31)
    c: Block(g25)
    c: Weight(g34) = 1
    c: Equal(g34,g35)
    c: Equal(g34,g36)
    c: InternalAlignment(g34,g37)
    c: InternalAlignment(g35,g37)
    c: InternalAlignment(g36,g37)
    c: InternalAlignment(g38,g37)
    c: InternalAlignment(g39,g37)
    c: Weight(g40) = 1
    c: Equal(g40,g41)
    c: Equal(g40,g42)
    c: InternalAlignment(g40,g43)
    c: InternalAlignment(g41,g43)
    c: InternalAlignment(g42,g43)
    c: InternalAlignment(g44,g43)
    c: InternalAlignment(g45,g43)
    c: Block(g37)
    c: Block(g43)
    c: Coincident(g46,g4)
    c: Coincident(g46,g3)
    c: Horizontal(g46)
    c: Distance(g46) = 450
    c: Coincident(g47,g4)
    c: Coincident(g47,g3)
    c: Horizontal(g47)
    c: Horizontal(g48)
    c: Coincident(g2,g48)
    c: Block(g48)
    c: Coincident(g1,g48)
    c: Weight(g49) = 1
    c: Equal(g49,g50)
    c: Equal(g49,g51)
    c: InternalAlignment(g49,g52)
    c: InternalAlignment(g50,g52)
    c: InternalAlignment(g51,g52)
    c: InternalAlignment(g53,g52)
    c: InternalAlignment(g54,g52)
    c: Block(g52)
    c: Weight(g55) = 1
    c: Equal(g55,g56)
    c: Equal(g55,g57)
    c: InternalAlignment(g55,g58)
    c: InternalAlignment(g56,g58)
    c: InternalAlignment(g57,g58)
    c: InternalAlignment(g59,g58)
    c: InternalAlignment(g60,g58)
    c: Block(g58)
    c: Weight(g61) = 1
    c: Equal(g61,g62)
    c: Equal(g61,g63)
    c: InternalAlignment(g61,g64)
    c: InternalAlignment(g62,g64)
    c: InternalAlignment(g63,g64)
    c: InternalAlignment(g65,g64)
    c: InternalAlignment(g66,g64)
    c: Block(g64)
    c: Weight(g67) = 1
    c: Equal(g67,g68)
    c: Equal(g67,g69)
    c: InternalAlignment(g67,g70)
    c: InternalAlignment(g68,g70)
    c: InternalAlignment(g69,g70)
    c: InternalAlignment(g71,g70)
    c: InternalAlignment(g72,g70)
    c: Block(g70)
    c: Weight(g73) = 1
    c: Equal(g73,g74)
    c: Equal(g73,g75)
    c: InternalAlignment(g73,g76)
    c: InternalAlignment(g74,g76)
    c: InternalAlignment(g75,g76)
    c: InternalAlignment(g77,g76)
    c: InternalAlignment(g78,g76)
    c: Weight(g79) = 1
    c: Equal(g79,g80)
    c: Equal(g79,g81)
    c: InternalAlignment(g79,g82)
    c: InternalAlignment(g80,g82)
    c: InternalAlignment(g81,g82)
    c: InternalAlignment(g83,g82)
    c: InternalAlignment(g84,g82)
    c: Block(g76)
    c: Block(g82)
    c: Coincident(g85,g76)
    c: Coincident(g85,g82)
    c: Vertical(g85)
    c: Coincident(g86,g76)
    c: Coincident(g86,g58)
    c: Coincident(g87,g58)
    c: Coincident(g87,g82)
    c: Weight(g88) = 1
    c: Equal(g88,g89)
    c: Equal(g88,g90)
    c: InternalAlignment(g88,g91)
    c: InternalAlignment(g89,g91)
    c: InternalAlignment(g90,g91)
    c: InternalAlignment(g92,g91)
    c: InternalAlignment(g93,g91)
    c: Weight(g94) = 1
    c: Equal(g94,g95)
    c: Equal(g94,g96)
    c: InternalAlignment(g94,g97)
    c: InternalAlignment(g95,g97)
    c: InternalAlignment(g96,g97)
    c: InternalAlignment(g98,g97)
    c: InternalAlignment(g99,g97)
    c: Block(g91)
    c: Block(g97)
    c: Coincident(g100,g91)
    c: Coincident(g100,g97)
    c: Vertical(g100)
    c: Coincident(g101,g91)
    c: Coincident(g101,g52)
    c: Coincident(g102,g52)
    c: Coincident(g102,g97)
    c: Weight(g103) = 1
    c: Equal(g103,g104)
    c: Equal(g103,g105)
    c: InternalAlignment(g103,g106)
    c: InternalAlignment(g104,g106)
    c: InternalAlignment(g105,g106)
    c: InternalAlignment(g107,g106)
    c: InternalAlignment(g108,g106)
    c: Weight(g109) = 1
    c: Equal(g109,g110)
    c: Equal(g109,g111)
    c: InternalAlignment(g109,g112)
    c: InternalAlignment(g110,g112)
    c: InternalAlignment(g111,g112)
    c: InternalAlignment(g113,g112)
    c: InternalAlignment(g114,g112)
    c: Block(g106)
    c: Block(g112)
    c: Coincident(g115,g106)
    c: Coincident(g115,g112)
    c: Vertical(g115)
    c: Coincident(g116,g112)
    c: Coincident(g116,g70)
    c: Coincident(g117,g70)
    c: Coincident(g117,g106)
    c: Weight(g118) = 1
    c: Equal(g118,g119)
    c: Equal(g118,g120)
    c: InternalAlignment(g118,g121)
    c: InternalAlignment(g119,g121)
    c: InternalAlignment(g120,g121)
    c: InternalAlignment(g122,g121)
    c: InternalAlignment(g123,g121)
    c: Weight(g124) = 1
    c: Equal(g124,g125)
    c: Equal(g124,g126)
    c: InternalAlignment(g124,g127)
    c: InternalAlignment(g125,g127)
    c: InternalAlignment(g126,g127)
    c: InternalAlignment(g128,g127)
    c: InternalAlignment(g129,g127)
    c: Block(g121)
    c: Block(g127)
    c: Coincident(g130,g121)
    c: Coincident(g130,g127)
    c: Vertical(g130)
    c: Coincident(g131,g127)
    c: Coincident(g131,g64)
    c: Coincident(g132,g64)
    c: Coincident(g132,g121)
    c: Weight(g133) = 1
    c: Equal(g133,g134)
    c: Equal(g133,g135)
    c: InternalAlignment(g133,g136)
    c: InternalAlignment(g134,g136)
    c: InternalAlignment(g135,g136)
    c: InternalAlignment(g137,g136)
    c: InternalAlignment(g138,g136)
    c: Weight(g139) = 1
    c: Equal(g139,g140)
    c: Equal(g139,g141)
    c: InternalAlignment(g139,g142)
    c: InternalAlignment(g140,g142)
    c: InternalAlignment(g141,g142)
    c: InternalAlignment(g143,g142)
    c: InternalAlignment(g144,g142)
    c: Weight(g145) = 1
    c: Equal(g145,g146)
    c: Equal(g145,g147)
    c: InternalAlignment(g145,g148)
    c: InternalAlignment(g146,g148)
    c: InternalAlignment(g147,g148)
    c: InternalAlignment(g149,g148)
    c: InternalAlignment(g150,g148)
    c: Weight(g151) = 1
    c: Equal(g151,g152)
    c: Equal(g151,g153)
    c: InternalAlignment(g151,g154)
    c: InternalAlignment(g152,g154)
    c: InternalAlignment(g153,g154)
    c: InternalAlignment(g155,g154)
    c: InternalAlignment(g156,g154)
    c: Block(g154)
    c: Block(g148)
    c: Block(g142)
    c: Block(g136)
    c: Coincident(g157,g31)
    c: Coincident(g157,g154)
    c: Coincident(g158,g154)
    c: Coincident(g158,g148)
    c: Horizontal(g158)
    c: Coincident(g159,g148)
    c: Coincident(g159,g31)
    c: Vertical(g159)
    c: Coincident(g160,g25)
    c: Coincident(g160,g142)
    c: Vertical(g160)
    c: Coincident(g161,g142)
    c: Coincident(g161,g136)
    c: Horizontal(g161)
    c: Coincident(g162,g136)
    c: Coincident(g162,g25)
    c: Weight(g163) = 1
    c: Equal(g163,g164)
    c: Equal(g163,g165)
    c: InternalAlignment(g163,g166)
    c: InternalAlignment(g164,g166)
    c: InternalAlignment(g165,g166)
    c: InternalAlignment(g167,g166)
    c: InternalAlignment(g168,g166)
    c: Weight(g169) = 1
    c: Equal(g169,g170)
    c: Equal(g169,g171)
    c: InternalAlignment(g169,g172)
    c: InternalAlignment(g170,g172)
    c: InternalAlignment(g171,g172)
    c: InternalAlignment(g173,g172)
    c: InternalAlignment(g174,g172)
    c: Weight(g175) = 1
    c: Equal(g175,g176)
    c: Equal(g175,g177)
    c: InternalAlignment(g175,g178)
    c: InternalAlignment(g176,g178)
    c: InternalAlignment(g177,g178)
    c: InternalAlignment(g179,g178)
    c: InternalAlignment(g180,g178)
    c: Weight(g181) = 1
    c: Equal(g181,g182)
    c: Equal(g181,g183)
    c: InternalAlignment(g181,g184)
    c: InternalAlignment(g182,g184)
    c: InternalAlignment(g183,g184)
    c: InternalAlignment(g185,g184)
    c: InternalAlignment(g186,g184)
    c: Block(g184)
    c: Block(g178)
    c: Block(g172)
    c: Block(g166)
    c: Coincident(g187,g184)
    c: Coincident(g187,g178)
    c: Horizontal(g187)
    c: Coincident(g188,g178)
    c: Coincident(g188,g13)
    c: Vertical(g188)
    c: Coincident(g189,g19)
    c: Coincident(g189,g172)
    c: Vertical(g189)
    c: Coincident(g190,g172)
    c: Coincident(g190,g166)
    c: Horizontal(g190)
    c: Coincident(g191,g166)
    c: Coincident(g191,g19)
    c: Coincident(g192,g13)
    c: Weight(g193) = 1
    c: Equal(g193,g194)
    c: Equal(g193,g195)
    c: InternalAlignment(g193,g196)
    c: InternalAlignment(g194,g196)
    c: InternalAlignment(g195,g196)
    c: InternalAlignment(g197,g196)
    c: InternalAlignment(g198,g196)
    c: Weight(g199) = 1
    c: Equal(g199,g200)
    c: Equal(g199,g201)
    c: InternalAlignment(g199,g202)
    c: InternalAlignment(g200,g202)
    c: InternalAlignment(g201,g202)
    c: InternalAlignment(g203,g202)
    c: InternalAlignment(g204,g202)
    c: Block(g202)
    c: Block(g196)
    c: Coincident(g205,g202)
    c: Coincident(g205,g37)
    c: Coincident(g206,g37)
    c: Coincident(g206,g196)
    c: Coincident(g207,g196)
    c: Coincident(g207,g202)
    c: Vertical(g207)
    c: Weight(g208) = 1
    c: Equal(g208,g209)
    c: Equal(g208,g210)
    c: InternalAlignment(g208,g211)
    c: InternalAlignment(g209,g211)
    c: InternalAlignment(g210,g211)
    c: InternalAlignment(g212,g211)
    c: InternalAlignment(g213,g211)
    c: Weight(g214) = 1
    c: Equal(g214,g215)
    c: Equal(g214,g216)
    c: InternalAlignment(g214,g217)
    c: InternalAlignment(g215,g217)
    c: InternalAlignment(g216,g217)
    c: InternalAlignment(g218,g217)
    c: InternalAlignment(g219,g217)
    c: Block(g217)
    c: Block(g211)
    c: Coincident(g220,g211)
    c: Coincident(g220,g43)
    c: Coincident(g221,g43)
    c: Coincident(g221,g217)
    c: Coincident(g222,g217)
    c: Coincident(g222,g211)
    c: Vertical(g222)
    c: Horizontal(g223)
    c: Block(g223)
    c: Vertical(g224)
    c: Block(g224)
    c: Block(g225)
    c: Weight(g226) = 1
    c: Equal(g226,g227)
    c: Equal(g226,g228)
    c: InternalAlignment(g226,g229)
    c: InternalAlignment(g227,g229)
    c: InternalAlignment(g228,g229)
    c: InternalAlignment(g230,g229)
    c: InternalAlignment(g231,g229)
    c: Weight(g232) = 1
    c: Equal(g232,g233)
    c: Equal(g232,g234)
    c: InternalAlignment(g232,g235)
    c: InternalAlignment(g233,g235)
    c: InternalAlignment(g234,g235)
    c: InternalAlignment(g236,g235)
    c: InternalAlignment(g237,g235)
    c: Weight(g238) = 1
    c: Equal(g238,g239)
    c: Equal(g238,g240)
    c: InternalAlignment(g238,g241)
    c: InternalAlignment(g239,g241)
    c: InternalAlignment(g240,g241)
    c: InternalAlignment(g242,g241)
    c: InternalAlignment(g243,g241)
    c: Weight(g244) = 1
    c: Equal(g244,g245)
    c: Equal(g244,g246)
    c: InternalAlignment(g244,g247)
    c: InternalAlignment(g245,g247)
    c: InternalAlignment(g246,g247)
    c: InternalAlignment(g248,g247)
    c: InternalAlignment(g249,g247)
    c: Block(g229)
    c: Block(g235)
    c: Block(g241)
    c: Block(g247)
    c: Coincident(g250,g235)
    c: Coincident(g250,g229)
    c: Horizontal(g250)
    c: Block(g192)
    c: Weight(g251) = 1
    c: Equal(g251,g252)
    c: Equal(g251,g253)
    c: InternalAlignment(g251,g254)
    c: InternalAlignment(g252,g254)
    c: InternalAlignment(g253,g254)
    c: InternalAlignment(g255,g254)
    c: InternalAlignment(g256,g254)
    c: Weight(g257) = 1
    c: Equal(g257,g258)
    c: Equal(g257,g259)
    c: InternalAlignment(g257,g260)
    c: InternalAlignment(g258,g260)
    c: InternalAlignment(g259,g260)
    c: InternalAlignment(g261,g260)
    c: InternalAlignment(g262,g260)
    c: Block(g254)
    c: Block(g260)
    c: Coincident(g263,g254)
    c: Coincident(g263,g260)
    c: Weight(g264) = 1
    c: Equal(g264,g265)
    c: Equal(g264,g266)
    c: InternalAlignment(g264,g267)
    c: InternalAlignment(g265,g267)
    c: InternalAlignment(g266,g267)
    c: InternalAlignment(g268,g267)
    c: InternalAlignment(g269,g267)
    c: Weight(g270) = 1
    c: Equal(g270,g271)
    c: Equal(g270,g272)
    c: InternalAlignment(g270,g273)
    c: InternalAlignment(g271,g273)
    c: InternalAlignment(g272,g273)
    c: InternalAlignment(g274,g273)
    c: InternalAlignment(g275,g273)
    c: Weight(g276) = 1
    c: Equal(g276,g277)
    c: Equal(g276,g278)
    c: InternalAlignment(g276,g279)
    c: InternalAlignment(g277,g279)
    c: InternalAlignment(g278,g279)
    c: InternalAlignment(g280,g279)
    c: InternalAlignment(g281,g279)
    c: Block(g279)
    c: Block(g273)
    c: Block(g267)
    c: Coincident(g282,g273)
    c: Coincident(g282,g267)
    c: Coincident(g283,g267)
    c: Coincident(g283,g279)
    c: Vertical(g283)
    c: Coincident(g284,g279)
    c: Coincident(g284,g273)
    c: Horizontal(g284)
    c: Weight(g285) = 1
    c: Equal(g285,g286)
    c: InternalAlignment(g285,g287)
    c: InternalAlignment(g286,g287)
    c: InternalAlignment(g288,g287)
    c: InternalAlignment(g289,g287)
    c: Weight(g290) = 1
    c: InternalAlignment(g291,g293)
    c: InternalAlignment(g292,g293)
    c: InternalAlignment(g294,g293)
    c: InternalAlignment(g295,g293)
    c: Weight(g296) = 1
    c: Equal(g296,g297)
    c: Equal(g296,g298)
    c: InternalAlignment(g296,g299)
    c: InternalAlignment(g297,g299)
    c: InternalAlignment(g298,g299)
    c: InternalAlignment(g300,g299)
    c: InternalAlignment(g301,g299)
    c: Equal(g302,g303)
    c: Equal(g302,g304)
    c: InternalAlignment(g302,g305)
    c: InternalAlignment(g303,g305)
    c: InternalAlignment(g304,g305)
    c: InternalAlignment(g306,g305)
    c: InternalAlignment(g307,g305)
    c: Block(g293)
    c: Block(g299)
    c: Block(g305)
    c: Block(g287)
    c: Coincident(g308,g287)
    c: Coincident(g308,g293)
    c: Horizontal(g308)
    c: Coincident(g309,g293)
    c: Coincident(g309,g299)
    c: Vertical(g309)
    c: Coincident(g310,g299)
    c: Coincident(g310,g305)
    c: Horizontal(g310)
    c: Coincident(g311,g305)
    c: Coincident(g311,g287)
    c: Weight(g312) = 1
    c: Equal(g312,g313)
    c: Equal(g312,g314)
    c: InternalAlignment(g312,g315)
    c: InternalAlignment(g313,g315)
    c: InternalAlignment(g314,g315)
    c: InternalAlignment(g316,g315)
    c: InternalAlignment(g317,g315)
    c: Weight(g318) = 1
    c: Equal(g318,g319)
    c: Equal(g318,g320)
    c: InternalAlignment(g318,g321)
    c: InternalAlignment(g319,g321)
    c: InternalAlignment(g320,g321)
    c: InternalAlignment(g322,g321)
    c: InternalAlignment(g323,g321)
    c: Weight(g324) = 1
    c: Equal(g324,g325)
    c: Equal(g324,g326)
    c: InternalAlignment(g324,g327)
    c: InternalAlignment(g325,g327)
    c: InternalAlignment(g326,g327)
    c: InternalAlignment(g328,g327)
    c: InternalAlignment(g329,g327)
    c: Block(g327)
    c: Block(g321)
    c: Block(g315)
    c: Coincident(g330,g327)
    c: Coincident(g330,g321)
    c: Horizontal(g330)
    c: Coincident(g331,g321)
    c: Coincident(g331,g315)
    c: Vertical(g331)
    c: Coincident(g332,g315)
    c: Coincident(g332,g327)
    c: InternalAlignment(g333,g334)
    c: InternalAlignment(g335,g334)
    c: InternalAlignment(g336,g334)
    c: Block(g334)
    c: Equal(g337,g338)
    c: Equal(g337,g339)
    c: InternalAlignment(g337,g340)
    c: InternalAlignment(g338,g340)
    c: InternalAlignment(g339,g340)
    c: InternalAlignment(g341,g340)
    c: InternalAlignment(g342,g340)
    c: Block(g340)
    c: Coincident(g343,g334)
    c: Horizontal(g343)
    c: Block(g343)
    c: Coincident(g344,g334)
    c: Coincident(g344,g260)
    c: Vertical(g344)
    c: Coincident(g345,g340)
    c: Coincident(g345,g254)
    c: Vertical(g345)
    c: Coincident(g347,g5)
    c: Coincident(g348,g5)
    c: Block(g346)
    c: Block(g5)
    c: Block(g348)
    c: Block(g347)
    c: Distance(g344) = 119.89
FEATURE [Sketcher::SketchObject] Sketch001
  FullyConstrained = true
  MapMode = 4
  Placement = pos=(0,0,0) rot=(0.57735,0.57735,0.57735;2.0944rad)
  Support = -> [Sketch]
  sketch-geometry (46):
    g0: BSplineCurve PolesCount=3 KnotsCount=2 Degree=2 IsPeriodic=0
    g1: ArcOfCircle CenterX=73.1223 CenterY=-32.291 CenterZ=0 NormalX=0 NormalY=0 NormalZ=1 AngleXU=0 Radius=13 StartAngle=5.92268 EndAngle=9.06428
    g2: ArcOfCircle CenterX=66.7816 CenterY=-49.1439 CenterZ=0 NormalX=0 NormalY=0 NormalZ=1 AngleXU=0 Radius=13 StartAngle=2.78068 EndAngle=5.92131
    g3: ArcOfCircle CenterX=55.9263 CenterY=-78.1807 CenterZ=0 NormalX=0 NormalY=0 NormalZ=1 AngleXU=0 Radius=13 StartAngle=5.92268 EndAngle=9.06428
    g4: ArcOfCircle CenterX=49.5884 CenterY=-95.0342 CenterZ=0 NormalX=0 NormalY=0 NormalZ=1 AngleXU=0 Radius=13 StartAngle=2.78068 EndAngle=5.92131
    g5: ArcOfCircle CenterX=38.7206 CenterY=-124.067 CenterZ=0 NormalX=0 NormalY=0 NormalZ=1 AngleXU=0 Radius=13 StartAngle=5.92268 EndAngle=9.06428
    g6: ArcOfCircle CenterX=32.3875 CenterY=-140.92 CenterZ=0 NormalX=0 NormalY=0 NormalZ=1 AngleXU=0 Radius=13 StartAngle=2.78068 EndAngle=5.92131
    g7: ArcOfCircle CenterX=21.4715 CenterY=-169.934 CenterZ=0 NormalX=0 NormalY=0 NormalZ=1 AngleXU=0 Radius=13 StartAngle=5.92268 EndAngle=9.06428
    g8: ArcOfCircle CenterX=15.1336 CenterY=-186.787 CenterZ=0 NormalX=0 NormalY=0 NormalZ=1 AngleXU=0 Radius=13 StartAngle=2.78068 EndAngle=5.92131
    g9-g12: Circle x4 (B-spline internal-alignment scaffolding for g13; pole/knot coordinates omitted)
    g13: BSplineCurve PolesCount=4 KnotsCount=2 Degree=3 IsPeriodic=0
    g14: GeomPoint X=28.8094 Y=-19.0875 Z=0
    g15: GeomPoint X=47.0443 Y=-50.4712 Z=0
    g16: Circle CenterX=53.5586 CenterY=-23.2695 CenterZ=0 NormalX=0 NormalY=0 NormalZ=1 AngleXU=0 Radius=3.24518
    g17: Circle CenterX=-195.441 CenterY=-127.082 CenterZ=0 NormalX=0 NormalY=0 NormalZ=1 AngleXU=0 Radius=1
    g18: Circle CenterX=-8.24091 CenterY=-197.481 CenterZ=0 NormalX=0 NormalY=0 NormalZ=1 AngleXU=0 Radius=1
    g19: Circle CenterX=12.8789 CenterY=-141.321 CenterZ=0 NormalX=0 NormalY=0 NormalZ=1 AngleXU=0 Radius=1
    g20: BSplineCurve PolesCount=3 KnotsCount=2 Degree=2 IsPeriodic=0
    g21: GeomPoint X=-195.441 Y=-127.082 Z=0
    g22: GeomPoint X=12.8789 Y=-141.321 Z=0
    g23: Circle CenterX=-12.8016 CenterY=-179.036 CenterZ=0 NormalX=0 NormalY=0 NormalZ=1 AngleXU=0 Radius=10.5072
    g24: Circle CenterX=0.933922 CenterY=-166.43 CenterZ=0 NormalX=0 NormalY=0 NormalZ=1 AngleXU=0 Radius=3.26661
    g25: Circle CenterX=-33.5518 CenterY=-176.44 CenterZ=0 NormalX=0 NormalY=0 NormalZ=1 AngleXU=0 Radius=5.64388
    g26: Circle CenterX=-47.2366 CenterY=-173.859 CenterZ=0 NormalX=0 NormalY=0 NormalZ=1 AngleXU=0 Radius=3.01653
    g27: Circle CenterX=-56.2595 CenterY=-171.456 CenterZ=0 NormalX=0 NormalY=0 NormalZ=1 AngleXU=0 Radius=2.12826
    g28: ArcOfCircle CenterX=51.2151 CenterY=-198.473 CenterZ=0 NormalX=0 NormalY=0 NormalZ=1 AngleXU=0 Radius=20 StartAngle=2.78189 EndAngle=4.35269
    g29: LineSegment StartX=32.4951 StartY=-191.433 StartZ=0 EndX=94.6578 EndY=-26.1352 EndZ=0
    g30: LineSegment StartX=43.1192 StartY=-220.001 StartZ=0 EndX=-196.497 EndY=-129.89 EndZ=0
    g31: LineSegment StartX=43.1192 StartY=-220.001 StartZ=0 EndX=44.1752 EndY=-217.193 EndZ=0
    g32: LineSegment StartX=117.223 StartY=-19.0875 StartZ=0 EndX=117.223 EndY=-16.0875 EndZ=0
    g33: LineSegment StartX=117.223 StartY=-16.0875 StartZ=0 EndX=17.2232 EndY=-16.0875 EndZ=0
    g34: LineSegment StartX=17.2232 StartY=-16.0875 StartZ=0 EndX=17.2232 EndY=-19.0875 EndZ=0
    g35: LineSegment StartX=28.8094 StartY=-19.0875 StartZ=0 EndX=17.2232 EndY=-19.0875 EndZ=0
    g36: LineSegment StartX=47.0443 StartY=-50.4712 StartZ=0 EndX=12.8789 EndY=-141.321 EndZ=0
    g37: LineSegment StartX=-195.441 StartY=-127.082 StartZ=0 EndX=-196.497 EndY=-129.89 EndZ=0
    g38: LineSegment StartX=85.2866 StartY=-36.8766 StartZ=0 EndX=78.9396 EndY=-53.7463 EndZ=0
    g39: LineSegment StartX=60.9579 StartY=-27.7053 StartZ=0 EndX=54.6191 EndY=-44.5532 EndZ=0
    g40: LineSegment StartX=68.0907 StartY=-82.7664 StartZ=0 EndX=61.7465 EndY=-99.6365 EndZ=0
    g41: LineSegment StartX=43.7619 StartY=-73.595 StartZ=0 EndX=37.426 EndY=-90.4435 EndZ=0
    g42: LineSegment StartX=50.885 StartY=-128.652 StartZ=0 EndX=44.5456 EndY=-145.522 EndZ=0
    g43: LineSegment StartX=26.5562 StartY=-119.481 StartZ=0 EndX=20.2251 EndY=-136.329 EndZ=0
    g44: LineSegment StartX=9.3071 StartY=-165.349 StartZ=0 EndX=2.97115 EndY=-182.197 EndZ=0
    g45: LineSegment StartX=33.6358 StartY=-174.52 StartZ=0 EndX=27.2917 EndY=-191.39 EndZ=0
  constraints (71):
    c: Block(g0)
    c: Block(g1)
    c: Block(g2)
    c: Block(g4)
    c: Block(g3)
    c: Block(g6)
    c: Block(g5)
    c: Block(g8)
    c: Block(g7)
    c: Weight(g9) = 1
    c: Equal(g9,g10)
    c: Equal(g9,g11)
    c: Equal(g9,g12)
    c: InternalAlignment(g9-g12 -> g13) x4
    c: InternalAlignment(g14,g13)
    c: InternalAlignment(g15,g13)
    c: Block(g16)
    c: Weight(g17) = 1
    c: Equal(g17,g18)
    c: Equal(g17,g19)
    c: InternalAlignment(g17,g20)
    c: InternalAlignment(g18,g20)
    c: InternalAlignment(g19,g20)
    c: InternalAlignment(g21,g20)
    c: InternalAlignment(g22,g20)
    c: Block(g20)
    c: Block(g23)
    c: Block(g24)
    c: Block(g25)
    c: Block(g26)
    c: Block(g27)
    c: Block(g28)
    c: Coincident(g29,g28)
    c: Coincident(g29,g0)
    c: Block(g13)
    c: Coincident(g31,g30)
    c: Coincident(g31,g28)
    c: Block(g31)
    c: Coincident(g32,g0)
    c: Vertical(g32)
    c: Coincident(g33,g32)
    c: Horizontal(g33)
    c: Coincident(g34,g33)
    c: Vertical(g34)
    c: Block(g33)
    c: Coincident(g35,g13)
    c: Coincident(g35,g34)
    c: Horizontal(g35)
    c: Coincident(g36,g13)
    c: Coincident(g36,g20)
    c: Coincident(g37,g20)
    c: Coincident(g37,g30)
    c: Block(g30)
    c: Coincident(g38,g1)
    c: Coincident(g38,g2)
    c: Coincident(g39,g1)
    c: Coincident(g39,g2)
    c: Coincident(g40,g3)
    c: Coincident(g40,g4)
    c: Coincident(g41,g3)
    c: Coincident(g41,g4)
    c: Coincident(g42,g5)
    c: Coincident(g42,g6)
    c: Coincident(g43,g5)
    c: Coincident(g43,g6)
    c: Coincident(g44,g7)
    c: Coincident(g44,g8)
    c: Coincident(g45,g7)
    c: Coincident(g45,g8)
    c: Distance(g30) = 256
    c: Distance(g33) = 100
FEATURE [Part::Extrusion] Extrude002
  Base = -> Sketch001
  Dir = (1,0,0)
  DirMode = 2
  FaceMakerClass = Part::FaceMakerBullseye
  LengthFwd = 8
  LengthRev = 0
  Solid = true
  Symmetric = false
FEATURE [Sketcher::SketchObject] Sketch002
  FullyConstrained = true
  sketch-geometry (20):
    g0: LineSegment StartX=-2.77179 StartY=-200.304 StartZ=0 EndX=5.22821 EndY=-200.304 EndZ=0
    g1: LineSegment StartX=5.22821 StartY=-200.304 StartZ=0 EndX=5.22821 EndY=-197.304 EndZ=0
    g2: LineSegment StartX=-2.77179 StartY=-200.304 StartZ=0 EndX=-2.77179 EndY=-197.304 EndZ=0
    g3: LineSegment StartX=5.22821 StartY=-197.304 StartZ=0 EndX=8.22821 EndY=-197.304 EndZ=0
    g4: LineSegment StartX=-2.77179 StartY=-197.304 StartZ=0 EndX=-5.77179 EndY=-197.304 EndZ=0
    g5: LineSegment StartX=19.2282 StartY=-203.304 StartZ=0 EndX=19.2282 EndY=-206.304 EndZ=0
    g6: LineSegment StartX=-16.7718 StartY=-203.304 StartZ=0 EndX=-16.7718 EndY=-206.304 EndZ=0
    g7: LineSegment StartX=-16.7718 StartY=-206.304 StartZ=0 EndX=19.2282 EndY=-206.304 EndZ=0
    g8: Circle CenterX=-16.7718 CenterY=-203.304 CenterZ=0 NormalX=0 NormalY=0 NormalZ=1 AngleXU=0 Radius=1
    g9: Circle CenterX=-5.77179 CenterY=-203.304 CenterZ=0 NormalX=0 NormalY=0 NormalZ=1 AngleXU=0 Radius=1
    g10: Circle CenterX=-5.77179 CenterY=-197.304 CenterZ=0 NormalX=0 NormalY=0 NormalZ=1 AngleXU=0 Radius=1
    g11: BSplineCurve PolesCount=3 KnotsCount=2 Degree=2 IsPeriodic=0
    g12: GeomPoint X=-16.7718 Y=-203.304 Z=0
    g13: GeomPoint X=-5.77179 Y=-197.304 Z=0
    g14: Circle CenterX=19.2282 CenterY=-203.304 CenterZ=0 NormalX=0 NormalY=0 NormalZ=1 AngleXU=0 Radius=1
    g15: Circle CenterX=8.22821 CenterY=-203.304 CenterZ=0 NormalX=0 NormalY=0 NormalZ=1 AngleXU=0 Radius=1
    g16: Circle CenterX=8.22821 CenterY=-197.304 CenterZ=0 NormalX=0 NormalY=0 NormalZ=1 AngleXU=0 Radius=1
    g17: BSplineCurve PolesCount=3 KnotsCount=2 Degree=2 IsPeriodic=0
    g18: GeomPoint X=19.2282 Y=-203.304 Z=0
    g19: GeomPoint X=8.22821 Y=-197.304 Z=0
  constraints (41):
    c: Horizontal(g0)
    c: Distance(g0) = 8
    c: Coincident(g1,g0)
    c: Vertical(g1)
    c: Distance(g1) = 3
    c: Coincident(g2,g0)
    c: Vertical(g2)
    c: Distance(g2) = 3
    c: Coincident(g3,g1)
    c: Horizontal(g3)
    c: Distance(g3) = 3
    c: Coincident(g4,g2)
    c: Horizontal(g4)
    c: Distance(g4) = 3
    c: Vertical(g5)
    c: Vertical(g6)
    c: Coincident(g7,g6)
    c: Coincident(g7,g5)
    c: Weight(g8) = 1
    c: Equal(g8,g9)
    c: Equal(g8,g10)
    c: Coincident(g11,g4)
    c: InternalAlignment(g8,g11)
    c: InternalAlignment(g9,g11)
    c: InternalAlignment(g10,g11)
    c: InternalAlignment(g12,g11)
    c: InternalAlignment(g13,g11)
    c: Coincident(g17,g5)
    c: Weight(g14) = 1
    c: Equal(g14,g15)
    c: Equal(g14,g16)
    c: Coincident(g17,g3)
    c: InternalAlignment(g14,g17)
    c: InternalAlignment(g15,g17)
    c: InternalAlignment(g16,g17)
    c: InternalAlignment(g18,g17)
    c: InternalAlignment(g19,g17)
    c: Block(g7)
    c: Block(g17)
    c: Block(g11)
    c: Block(g6)
FEATURE [Part::Extrusion] Extrude003
  Base = -> Sketch002
  Dir = (0,0,1)
  DirMode = 2
  FaceMakerClass = Part::FaceMakerBullseye
  LengthFwd = 260
  LengthRev = 0
  Solid = true
  Symmetric = false
FEATURE [Sketcher::SketchObject] Sketch003
  FullyConstrained = false
  sketch-geometry (375):
    g0: LineSegment StartX=-42.9272 StartY=136.221 StartZ=0 EndX=-42.9272 EndY=-103.779 EndZ=0
    g1: LineSegment StartX=407.073 StartY=136.221 StartZ=0 EndX=407.073 EndY=-103.779 EndZ=0
    g2: ArcOfCircle CenterX=-26.9272 CenterY=-83.7794 CenterZ=0 NormalX=0 NormalY=0 NormalZ=1 AngleXU=0 Radius=8 StartAngle=3.14159 EndAngle=6.28319
    g3: ArcOfCircle CenterX=391.073 CenterY=-83.7794 CenterZ=0 NormalX=0 NormalY=0 NormalZ=1 AngleXU=0 Radius=8 StartAngle=3.14159 EndAngle=6.28319
    g4: Circle CenterX=175.022 CenterY=27.0628 CenterZ=0 NormalX=0 NormalY=0 NormalZ=1 AngleXU=0 Radius=1
    g5: Circle CenterX=179.022 CenterY=24.8665 CenterZ=0 NormalX=0 NormalY=0 NormalZ=1 AngleXU=0 Radius=1
    g6: Circle CenterX=179.022 CenterY=27.0628 CenterZ=0 NormalX=0 NormalY=0 NormalZ=1 AngleXU=0 Radius=1
    g7: BSplineCurve PolesCount=3 KnotsCount=2 Degree=2 IsPeriodic=0
    g8: GeomPoint X=175.022 Y=27.0628 Z=0
    g9: GeomPoint X=179.022 Y=27.0628 Z=0
    g10: Circle CenterX=189.124 CenterY=27.0628 CenterZ=0 NormalX=0 NormalY=0 NormalZ=1 AngleXU=0 Radius=1
    g11: Circle CenterX=185.124 CenterY=24.8665 CenterZ=0 NormalX=0 NormalY=0 NormalZ=1 AngleXU=0 Radius=1
    g12: Circle CenterX=185.124 CenterY=27.0628 CenterZ=0 NormalX=0 NormalY=0 NormalZ=1 AngleXU=0 Radius=1
    g13: BSplineCurve PolesCount=3 KnotsCount=2 Degree=2 IsPeriodic=0
    g14: GeomPoint X=189.124 Y=27.0628 Z=0
    g15: GeomPoint X=185.124 Y=27.0628 Z=0
    g16: Circle CenterX=175.022 CenterY=5.37834 CenterZ=0 NormalX=0 NormalY=0 NormalZ=1 AngleXU=0 Radius=1
    g17: Circle CenterX=179.022 CenterY=7.57463 CenterZ=0 NormalX=0 NormalY=0 NormalZ=1 AngleXU=0 Radius=1
    g18: Circle CenterX=179.022 CenterY=5.34704 CenterZ=0 NormalX=0 NormalY=0 NormalZ=1 AngleXU=0 Radius=1
    g19: BSplineCurve PolesCount=3 KnotsCount=2 Degree=2 IsPeriodic=0
    g20: GeomPoint X=175.022 Y=5.37834 Z=0
    g21: GeomPoint X=179.022 Y=5.34704 Z=0
    g22: Circle CenterX=189.124 CenterY=5.37834 CenterZ=0 NormalX=0 NormalY=0 NormalZ=1 AngleXU=0 Radius=1
    g23: Circle CenterX=185.124 CenterY=7.57463 CenterZ=0 NormalX=0 NormalY=0 NormalZ=1 AngleXU=0 Radius=1
    g24: Circle CenterX=185.124 CenterY=5.34704 CenterZ=0 NormalX=0 NormalY=0 NormalZ=1 AngleXU=0 Radius=1
    g25: BSplineCurve PolesCount=3 KnotsCount=2 Degree=2 IsPeriodic=0
    g26: GeomPoint X=189.124 Y=5.37834 Z=0
    g27: GeomPoint X=185.124 Y=5.34704 Z=0
    g28: Circle CenterX=165.871 CenterY=18.1458 CenterZ=0 NormalX=0 NormalY=0 NormalZ=1 AngleXU=0 Radius=1
    g29: Circle CenterX=169.377 CenterY=16.2206 CenterZ=0 NormalX=0 NormalY=0 NormalZ=1 AngleXU=0 Radius=1
    g30: Circle CenterX=165.871 CenterY=14.2954 CenterZ=0 NormalX=0 NormalY=0 NormalZ=1 AngleXU=0 Radius=1
    g31: BSplineCurve PolesCount=3 KnotsCount=2 Degree=2 IsPeriodic=0
    g32: GeomPoint X=165.871 Y=18.1458 Z=0
    g33: GeomPoint X=165.871 Y=14.2954 Z=0
    g34: Circle CenterX=198.275 CenterY=18.1458 CenterZ=0 NormalX=0 NormalY=0 NormalZ=1 AngleXU=0 Radius=1
    g35: Circle CenterX=194.768 CenterY=16.2206 CenterZ=0 NormalX=0 NormalY=0 NormalZ=1 AngleXU=0 Radius=1
    g36: Circle CenterX=198.275 CenterY=14.2954 CenterZ=0 NormalX=0 NormalY=0 NormalZ=1 AngleXU=0 Radius=1
    g37: BSplineCurve PolesCount=3 KnotsCount=2 Degree=2 IsPeriodic=0
    g38: GeomPoint X=198.275 Y=18.1458 Z=0
    g39: GeomPoint X=198.275 Y=14.2954 Z=0
    g40: LineSegment StartX=407.073 StartY=-103.779 StartZ=0 EndX=-42.9272 EndY=-103.779 EndZ=0
    g41: Circle CenterX=125.607 CenterY=54.1951 CenterZ=0 NormalX=0 NormalY=0 NormalZ=1 AngleXU=0 Radius=1
    g42: Circle CenterX=139.632 CenterY=46.4944 CenterZ=0 NormalX=0 NormalY=0 NormalZ=1 AngleXU=0 Radius=1
    g43: Circle CenterX=127.326 CenterY=56.7187 CenterZ=0 NormalX=0 NormalY=0 NormalZ=1 AngleXU=0 Radius=1
    g44: BSplineCurve PolesCount=3 KnotsCount=2 Degree=2 IsPeriodic=0
    g45: GeomPoint X=125.607 Y=54.1951 Z=0
    g46: GeomPoint X=127.326 Y=56.7187 Z=0
    g47: Circle CenterX=236.821 CenterY=56.7187 CenterZ=0 NormalX=0 NormalY=0 NormalZ=1 AngleXU=0 Radius=1
    g48: Circle CenterX=224.513 CenterY=46.4944 CenterZ=0 NormalX=0 NormalY=0 NormalZ=1 AngleXU=0 Radius=1
    g49: Circle CenterX=238.538 CenterY=54.1951 CenterZ=0 NormalX=0 NormalY=0 NormalZ=1 AngleXU=0 Radius=1
    g50: BSplineCurve PolesCount=3 KnotsCount=2 Degree=2 IsPeriodic=0
    g51: GeomPoint X=236.821 Y=56.7187 Z=0
    g52: GeomPoint X=238.538 Y=54.1951 Z=0
    g53: Circle CenterX=238.538 CenterY=-21.7539 CenterZ=0 NormalX=0 NormalY=0 NormalZ=1 AngleXU=0 Radius=1
    g54: Circle CenterX=224.513 CenterY=-14.0532 CenterZ=0 NormalX=0 NormalY=0 NormalZ=1 AngleXU=0 Radius=1
    g55: Circle CenterX=236.821 CenterY=-24.2775 CenterZ=0 NormalX=0 NormalY=0 NormalZ=1 AngleXU=0 Radius=1
    g56: BSplineCurve PolesCount=3 KnotsCount=2 Degree=2 IsPeriodic=0
    g57: GeomPoint X=238.538 Y=-21.7539 Z=0
    g58: GeomPoint X=236.821 Y=-24.2775 Z=0
    g59: Circle CenterX=125.607 CenterY=-21.7539 CenterZ=0 NormalX=0 NormalY=0 NormalZ=1 AngleXU=0 Radius=1
    g60: Circle CenterX=139.632 CenterY=-14.0532 CenterZ=0 NormalX=0 NormalY=0 NormalZ=1 AngleXU=0 Radius=1
    g61: Circle CenterX=127.325 CenterY=-24.2775 CenterZ=0 NormalX=0 NormalY=0 NormalZ=1 AngleXU=0 Radius=1
    g62: BSplineCurve PolesCount=3 KnotsCount=2 Degree=2 IsPeriodic=0
    g63: GeomPoint X=125.607 Y=-21.7539 Z=0
    g64: GeomPoint X=127.325 Y=-24.2775 Z=0
    g65: Circle CenterX=302.996 CenterY=111.695 CenterZ=0 NormalX=0 NormalY=0 NormalZ=1 AngleXU=0 Radius=1
    g66: Circle CenterX=306.073 CenterY=114.251 CenterZ=0 NormalX=0 NormalY=0 NormalZ=1 AngleXU=0 Radius=1
    g67: Circle CenterX=306.073 CenterY=110.251 CenterZ=0 NormalX=0 NormalY=0 NormalZ=1 AngleXU=0 Radius=1
    g68: BSplineCurve PolesCount=3 KnotsCount=2 Degree=2 IsPeriodic=0
    g69: GeomPoint X=302.996 Y=111.695 Z=0
    g70: GeomPoint X=306.073 Y=110.251 Z=0
    g71: Circle CenterX=306.073 CenterY=95.2763 CenterZ=0 NormalX=0 NormalY=0 NormalZ=1 AngleXU=0 Radius=1
    g72: Circle CenterX=306.073 CenterY=91.2763 CenterZ=0 NormalX=0 NormalY=0 NormalZ=1 AngleXU=0 Radius=1
    g73: Circle CenterX=302.567 CenterY=89.3511 CenterZ=0 NormalX=0 NormalY=0 NormalZ=1 AngleXU=0 Radius=1
    g74: BSplineCurve PolesCount=3 KnotsCount=2 Degree=2 IsPeriodic=0
    g75: GeomPoint X=306.073 Y=95.2763 Z=0
    g76: GeomPoint X=302.567 Y=89.3511 Z=0
    g77: LineSegment StartX=306.073 StartY=110.251 StartZ=0 EndX=306.073 EndY=95.2763 EndZ=0
    g78: LineSegment StartX=302.996 StartY=111.695 StartZ=0 EndX=236.821 EndY=56.7187 EndZ=0
    g79: LineSegment StartX=238.538 StartY=54.1951 StartZ=0 EndX=302.567 EndY=89.3511 EndZ=0
    g80: Circle CenterX=61.1496 CenterY=111.695 CenterZ=0 NormalX=0 NormalY=0 NormalZ=1 AngleXU=0 Radius=1
    g81: Circle CenterX=58.0728 CenterY=114.251 CenterZ=0 NormalX=0 NormalY=0 NormalZ=1 AngleXU=0 Radius=1
    g82: Circle CenterX=58.0728 CenterY=110.251 CenterZ=0 NormalX=0 NormalY=0 NormalZ=1 AngleXU=0 Radius=1
    g83: BSplineCurve PolesCount=3 KnotsCount=2 Degree=2 IsPeriodic=0
    g84: GeomPoint X=61.1496 Y=111.695 Z=0
    g85: GeomPoint X=58.0728 Y=110.251 Z=0
    g86: Circle CenterX=61.5791 CenterY=89.3511 CenterZ=0 NormalX=0 NormalY=0 NormalZ=1 AngleXU=0 Radius=1
    g87: Circle CenterX=58.0728 CenterY=91.2763 CenterZ=0 NormalX=0 NormalY=0 NormalZ=1 AngleXU=0 Radius=1
    g88: Circle CenterX=58.0728 CenterY=95.2763 CenterZ=0 NormalX=0 NormalY=0 NormalZ=1 AngleXU=0 Radius=1
    g89: BSplineCurve PolesCount=3 KnotsCount=2 Degree=2 IsPeriodic=0
    g90: GeomPoint X=61.5791 Y=89.3511 Z=0
    g91: GeomPoint X=58.0728 Y=95.2763 Z=0
    g92: LineSegment StartX=58.0728 StartY=110.251 StartZ=0 EndX=58.0728 EndY=95.2763 EndZ=0
    g93: LineSegment StartX=61.1496 StartY=111.695 StartZ=0 EndX=127.326 EndY=56.7187 EndZ=0
    g94: LineSegment StartX=125.607 StartY=54.1951 StartZ=0 EndX=61.5791 EndY=89.3511 EndZ=0
    g95: Circle CenterX=61.5791 CenterY=-56.9099 CenterZ=0 NormalX=0 NormalY=0 NormalZ=1 AngleXU=0 Radius=1
    g96: Circle CenterX=58.0728 CenterY=-58.8351 CenterZ=0 NormalX=0 NormalY=0 NormalZ=1 AngleXU=0 Radius=1
    g97: Circle CenterX=58.0728 CenterY=-62.8351 CenterZ=0 NormalX=0 NormalY=0 NormalZ=1 AngleXU=0 Radius=1
    g98: BSplineCurve PolesCount=3 KnotsCount=2 Degree=2 IsPeriodic=0
    g99: GeomPoint X=61.5791 Y=-56.9099 Z=0
    g100: GeomPoint X=58.0728 Y=-62.8351 Z=0
    g101: Circle CenterX=58.0728 CenterY=-77.8102 CenterZ=0 NormalX=0 NormalY=0 NormalZ=1 AngleXU=0 Radius=1
    g102: Circle CenterX=58.0728 CenterY=-81.8102 CenterZ=0 NormalX=0 NormalY=0 NormalZ=1 AngleXU=0 Radius=1
    g103: Circle CenterX=61.1496 CenterY=-79.2541 CenterZ=0 NormalX=0 NormalY=0 NormalZ=1 AngleXU=0 Radius=1
    g104: BSplineCurve PolesCount=3 KnotsCount=2 Degree=2 IsPeriodic=0
    g105: GeomPoint X=58.0728 Y=-77.8102 Z=0
    g106: GeomPoint X=61.1496 Y=-79.2541 Z=0
    g107: LineSegment StartX=58.0728 StartY=-62.8351 StartZ=0 EndX=58.0728 EndY=-77.8102 EndZ=0
    g108: LineSegment StartX=61.1496 StartY=-79.2541 StartZ=0 EndX=127.325 EndY=-24.2775 EndZ=0
    g109: LineSegment StartX=125.607 StartY=-21.7539 StartZ=0 EndX=61.5791 EndY=-56.9099 EndZ=0
    g110: Circle CenterX=302.567 CenterY=-56.9099 CenterZ=0 NormalX=0 NormalY=0 NormalZ=1 AngleXU=0 Radius=1
    g111: Circle CenterX=306.073 CenterY=-58.8351 CenterZ=0 NormalX=0 NormalY=0 NormalZ=1 AngleXU=0 Radius=1
    g112: Circle CenterX=306.073 CenterY=-62.8351 CenterZ=0 NormalX=0 NormalY=0 NormalZ=1 AngleXU=0 Radius=1
    g113: BSplineCurve PolesCount=3 KnotsCount=2 Degree=2 IsPeriodic=0
    g114: GeomPoint X=302.567 Y=-56.9099 Z=0
    g115: GeomPoint X=306.073 Y=-62.8351 Z=0
    g116: Circle CenterX=302.996 CenterY=-79.2541 CenterZ=0 NormalX=0 NormalY=0 NormalZ=1 AngleXU=0 Radius=1
    g117: Circle CenterX=306.073 CenterY=-81.8102 CenterZ=0 NormalX=0 NormalY=0 NormalZ=1 AngleXU=0 Radius=1
    g118: Circle CenterX=306.073 CenterY=-77.8102 CenterZ=0 NormalX=0 NormalY=0 NormalZ=1 AngleXU=0 Radius=1
    g119: BSplineCurve PolesCount=3 KnotsCount=2 Degree=2 IsPeriodic=0
    g120: GeomPoint X=302.996 Y=-79.2541 Z=0
    g121: GeomPoint X=306.073 Y=-77.8102 Z=0
    g122: LineSegment StartX=306.073 StartY=-62.8351 StartZ=0 EndX=306.073 EndY=-77.8102 EndZ=0
    g123: LineSegment StartX=302.996 StartY=-79.2541 StartZ=0 EndX=236.821 EndY=-24.2775 EndZ=0
    g124: LineSegment StartX=238.538 StartY=-21.7539 StartZ=0 EndX=302.567 EndY=-56.9099 EndZ=0
    g125: Circle CenterX=61.6457 CenterY=-88.8112 CenterZ=0 NormalX=0 NormalY=0 NormalZ=1 AngleXU=0 Radius=1
    g126: Circle CenterX=58.0728 CenterY=-91.7794 CenterZ=0 NormalX=0 NormalY=0 NormalZ=1 AngleXU=0 Radius=1
    g127: Circle CenterX=63.9135 CenterY=-91.7794 CenterZ=0 NormalX=0 NormalY=0 NormalZ=1 AngleXU=0 Radius=1
    g128: BSplineCurve PolesCount=3 KnotsCount=2 Degree=2 IsPeriodic=0
    g129: GeomPoint X=61.6457 Y=-88.8112 Z=0
    g130: GeomPoint X=63.9135 Y=-91.7794 Z=0
    g131: Circle CenterX=179.022 CenterY=-85.8163 CenterZ=0 NormalX=0 NormalY=0 NormalZ=1 AngleXU=0 Radius=1
    g132: Circle CenterX=179.022 CenterY=-91.7794 CenterZ=0 NormalX=0 NormalY=0 NormalZ=1 AngleXU=0 Radius=1
    g133: Circle CenterX=171.895 CenterY=-91.7794 CenterZ=0 NormalX=0 NormalY=0 NormalZ=1 AngleXU=0 Radius=1
    g134: BSplineCurve PolesCount=3 KnotsCount=2 Degree=2 IsPeriodic=0
    g135: GeomPoint X=179.022 Y=-85.8163 Z=0
    g136: GeomPoint X=171.895 Y=-91.7794 Z=0
    g137: Circle CenterX=185.124 CenterY=-86.2028 CenterZ=0 NormalX=0 NormalY=0 NormalZ=1 AngleXU=0 Radius=1
    g138: Circle CenterX=185.124 CenterY=-91.7794 CenterZ=0 NormalX=0 NormalY=0 NormalZ=1 AngleXU=0 Radius=1
    g139: Circle CenterX=191.747 CenterY=-91.7794 CenterZ=0 NormalX=0 NormalY=0 NormalZ=1 AngleXU=0 Radius=1
    g140: BSplineCurve PolesCount=3 KnotsCount=2 Degree=2 IsPeriodic=0
    g141: GeomPoint X=185.124 Y=-86.2028 Z=0
    g142: GeomPoint X=191.747 Y=-91.7794 Z=0
    g143: Circle CenterX=299.888 CenterY=-86.6413 CenterZ=0 NormalX=0 NormalY=0 NormalZ=1 AngleXU=0 Radius=1
    g144: Circle CenterX=306.073 CenterY=-91.7794 CenterZ=0 NormalX=0 NormalY=0 NormalZ=1 AngleXU=0 Radius=1
    g145: Circle CenterX=298.776 CenterY=-91.7794 CenterZ=0 NormalX=0 NormalY=0 NormalZ=1 AngleXU=0 Radius=1
    g146: BSplineCurve PolesCount=3 KnotsCount=2 Degree=2 IsPeriodic=0
    g147: GeomPoint X=299.888 Y=-86.6413 Z=0
    g148: GeomPoint X=298.776 Y=-91.7794 Z=0
    g149: LineSegment StartX=189.124 StartY=5.37834 StartZ=0 EndX=299.888 EndY=-86.6413 EndZ=0
    g150: LineSegment StartX=298.776 StartY=-91.7794 StartZ=0 EndX=191.747 EndY=-91.7794 EndZ=0
    g151: LineSegment StartX=185.124 StartY=-86.2028 StartZ=0 EndX=185.124 EndY=5.34704 EndZ=0
    g152: LineSegment StartX=179.022 StartY=5.34704 StartZ=0 EndX=179.022 EndY=-85.8163 EndZ=0
    g153: LineSegment StartX=171.895 StartY=-91.7794 StartZ=0 EndX=63.9135 EndY=-91.7794 EndZ=0
    g154: LineSegment StartX=61.6457 StartY=-88.8112 StartZ=0 EndX=175.022 EndY=5.37834 EndZ=0
    g155: Circle CenterX=302.073 CenterY=124.221 CenterZ=0 NormalX=0 NormalY=0 NormalZ=1 AngleXU=0 Radius=1
    g156: Circle CenterX=306.073 CenterY=124.221 CenterZ=0 NormalX=0 NormalY=0 NormalZ=1 AngleXU=0 Radius=1
    g157: Circle CenterX=302.996 CenterY=121.665 CenterZ=0 NormalX=0 NormalY=0 NormalZ=1 AngleXU=0 Radius=1
    g158: BSplineCurve PolesCount=3 KnotsCount=2 Degree=2 IsPeriodic=0
    g159: GeomPoint X=302.073 Y=124.221 Z=0
    g160: GeomPoint X=302.996 Y=121.665 Z=0
    g161: Circle CenterX=189.124 CenterY=124.221 CenterZ=0 NormalX=0 NormalY=0 NormalZ=1 AngleXU=0 Radius=1
    g162: Circle CenterX=185.124 CenterY=124.221 CenterZ=0 NormalX=0 NormalY=0 NormalZ=1 AngleXU=0 Radius=1
    g163: Circle CenterX=185.124 CenterY=120.221 CenterZ=0 NormalX=0 NormalY=0 NormalZ=1 AngleXU=0 Radius=1
    g164: BSplineCurve PolesCount=3 KnotsCount=2 Degree=2 IsPeriodic=0
    g165: GeomPoint X=189.124 Y=124.221 Z=0
    g166: GeomPoint X=185.124 Y=120.221 Z=0
    g167: Circle CenterX=175.022 CenterY=124.221 CenterZ=0 NormalX=0 NormalY=0 NormalZ=1 AngleXU=0 Radius=1
    g168: Circle CenterX=179.022 CenterY=124.221 CenterZ=0 NormalX=0 NormalY=0 NormalZ=1 AngleXU=0 Radius=1
    g169: Circle CenterX=179.022 CenterY=120.221 CenterZ=0 NormalX=0 NormalY=0 NormalZ=1 AngleXU=0 Radius=1
    g170: BSplineCurve PolesCount=3 KnotsCount=2 Degree=2 IsPeriodic=0
    g171: GeomPoint X=175.022 Y=124.221 Z=0
    g172: GeomPoint X=179.022 Y=120.221 Z=0
    g173: Circle CenterX=62.0728 CenterY=124.221 CenterZ=0 NormalX=0 NormalY=0 NormalZ=1 AngleXU=0 Radius=1
    g174: Circle CenterX=58.0728 CenterY=124.221 CenterZ=0 NormalX=0 NormalY=0 NormalZ=1 AngleXU=0 Radius=1
    g175: Circle CenterX=61.1496 CenterY=121.665 CenterZ=0 NormalX=0 NormalY=0 NormalZ=1 AngleXU=0 Radius=1
    g176: BSplineCurve PolesCount=3 KnotsCount=2 Degree=2 IsPeriodic=0
    g177: GeomPoint X=62.0728 Y=124.221 Z=0
    g178: GeomPoint X=61.1496 Y=121.665 Z=0
    g179: LineSegment StartX=62.0728 StartY=124.221 StartZ=0 EndX=175.022 EndY=124.221 EndZ=0
    g180: LineSegment StartX=179.022 StartY=120.221 StartZ=0 EndX=179.022 EndY=27.0628 EndZ=0
    g181: LineSegment StartX=185.124 StartY=27.0628 StartZ=0 EndX=185.124 EndY=120.221 EndZ=0
    g182: LineSegment StartX=189.124 StartY=124.221 StartZ=0 EndX=302.073 EndY=124.221 EndZ=0
    g183: LineSegment StartX=302.996 StartY=121.665 StartZ=0 EndX=189.124 EndY=27.0628 EndZ=0
    g184: LineSegment StartX=175.022 StartY=27.0628 StartZ=0 EndX=61.1496 EndY=121.665 EndZ=0
    g185: Circle CenterX=61.5791 CenterY=75.4095 CenterZ=0 NormalX=0 NormalY=0 NormalZ=1 AngleXU=0 Radius=1
    g186: Circle CenterX=58.0728 CenterY=77.3346 CenterZ=0 NormalX=0 NormalY=0 NormalZ=1 AngleXU=0 Radius=1
    g187: Circle CenterX=58.0728 CenterY=73.3346 CenterZ=0 NormalX=0 NormalY=0 NormalZ=1 AngleXU=0 Radius=1
    g188: BSplineCurve PolesCount=3 KnotsCount=2 Degree=2 IsPeriodic=0
    g189: GeomPoint X=61.5791 Y=75.4095 Z=0
    g190: GeomPoint X=58.0728 Y=73.3346 Z=0
    g191: Circle CenterX=58.0728 CenterY=-40.8935 CenterZ=0 NormalX=0 NormalY=0 NormalZ=1 AngleXU=0 Radius=1
    g192: Circle CenterX=58.0728 CenterY=-44.8935 CenterZ=0 NormalX=0 NormalY=0 NormalZ=1 AngleXU=0 Radius=1
    g193: Circle CenterX=61.5791 CenterY=-42.9683 CenterZ=0 NormalX=0 NormalY=0 NormalZ=1 AngleXU=0 Radius=1
    g194: BSplineCurve PolesCount=3 KnotsCount=2 Degree=2 IsPeriodic=0
    g195: GeomPoint X=58.0728 Y=-40.8935 Z=0
    g196: GeomPoint X=61.5791 Y=-42.9683 Z=0
    g197: LineSegment StartX=61.5791 StartY=-42.9683 StartZ=0 EndX=165.871 EndY=14.2954 EndZ=0
    g198: LineSegment StartX=165.871 StartY=18.1458 StartZ=0 EndX=61.5791 EndY=75.4095 EndZ=0
    g199: LineSegment StartX=58.0728 StartY=73.3346 StartZ=0 EndX=58.0728 EndY=-40.8935 EndZ=0
    g200: Circle CenterX=302.567 CenterY=-42.9683 CenterZ=0 NormalX=0 NormalY=0 NormalZ=1 AngleXU=0 Radius=1
    g201: Circle CenterX=306.073 CenterY=-44.8935 CenterZ=0 NormalX=0 NormalY=0 NormalZ=1 AngleXU=0 Radius=1
    g202: Circle CenterX=306.073 CenterY=-40.8935 CenterZ=0 NormalX=0 NormalY=0 NormalZ=1 AngleXU=0 Radius=1
    g203: BSplineCurve PolesCount=3 KnotsCount=2 Degree=2 IsPeriodic=0
    g204: GeomPoint X=302.567 Y=-42.9683 Z=0
    g205: GeomPoint X=306.073 Y=-40.8935 Z=0
    g206: Circle CenterX=306.073 CenterY=73.3346 CenterZ=0 NormalX=0 NormalY=0 NormalZ=1 AngleXU=0 Radius=1
    g207: Circle CenterX=306.073 CenterY=77.3346 CenterZ=0 NormalX=0 NormalY=0 NormalZ=1 AngleXU=0 Radius=1
    g208: Circle CenterX=302.567 CenterY=75.4095 CenterZ=0 NormalX=0 NormalY=0 NormalZ=1 AngleXU=0 Radius=1
    g209: BSplineCurve PolesCount=3 KnotsCount=2 Degree=2 IsPeriodic=0
    g210: GeomPoint X=306.073 Y=73.3346 Z=0
    g211: GeomPoint X=302.567 Y=75.4095 Z=0
    g212: LineSegment StartX=302.567 StartY=-42.9683 StartZ=0 EndX=198.275 EndY=14.2954 EndZ=0
    g213: LineSegment StartX=198.275 StartY=18.1458 StartZ=0 EndX=302.567 EndY=75.4095 EndZ=0
    g214: LineSegment StartX=306.073 StartY=73.3346 StartZ=0 EndX=306.073 EndY=-40.8935 EndZ=0
    g215: LineSegment StartX=322.073 StartY=105.865 StartZ=0 EndX=328.643 EndY=105.865 EndZ=0
    g216: LineSegment StartX=318.073 StartY=120.221 StartZ=0 EndX=318.073 EndY=109.865 EndZ=0
    g217: LineSegment StartX=336.157 StartY=107.779 StartZ=0 EndX=362.567 EndY=122.294 EndZ=0
    g218: Circle CenterX=362.073 CenterY=124.221 CenterZ=0 NormalX=0 NormalY=0 NormalZ=1 AngleXU=0 Radius=1
    g219: Circle CenterX=366.073 CenterY=124.221 CenterZ=0 NormalX=0 NormalY=0 NormalZ=1 AngleXU=0 Radius=1
    g220: Circle CenterX=362.567 CenterY=122.294 CenterZ=0 NormalX=0 NormalY=0 NormalZ=1 AngleXU=0 Radius=1
    g221: BSplineCurve PolesCount=3 KnotsCount=2 Degree=2 IsPeriodic=0
    g222: GeomPoint X=362.073 Y=124.221 Z=0
    g223: GeomPoint X=362.567 Y=122.294 Z=0
    g224: Circle CenterX=322.073 CenterY=124.221 CenterZ=0 NormalX=0 NormalY=0 NormalZ=1 AngleXU=0 Radius=1
    g225: Circle CenterX=318.073 CenterY=124.221 CenterZ=0 NormalX=0 NormalY=0 NormalZ=1 AngleXU=0 Radius=1
    g226: Circle CenterX=318.073 CenterY=120.221 CenterZ=0 NormalX=0 NormalY=0 NormalZ=1 AngleXU=0 Radius=1
    g227: BSplineCurve PolesCount=3 KnotsCount=2 Degree=2 IsPeriodic=0
    g228: GeomPoint X=322.073 Y=124.221 Z=0
    g229: GeomPoint X=318.073 Y=120.221 Z=0
    g230: Circle CenterX=322.073 CenterY=105.865 CenterZ=0 NormalX=0 NormalY=0 NormalZ=1 AngleXU=0 Radius=1
    g231: Circle CenterX=318.073 CenterY=105.865 CenterZ=0 NormalX=0 NormalY=0 NormalZ=1 AngleXU=0 Radius=1
    g232: Circle CenterX=318.073 CenterY=109.865 CenterZ=0 NormalX=0 NormalY=0 NormalZ=1 AngleXU=0 Radius=1
    g233: BSplineCurve PolesCount=3 KnotsCount=2 Degree=2 IsPeriodic=0
    g234: GeomPoint X=322.073 Y=105.865 Z=0
    g235: GeomPoint X=318.073 Y=109.865 Z=0
    g236: Circle CenterX=336.157 CenterY=107.779 CenterZ=0 NormalX=0 NormalY=0 NormalZ=1 AngleXU=0 Radius=1
    g237: Circle CenterX=332.651 CenterY=105.853 CenterZ=0 NormalX=0 NormalY=0 NormalZ=1 AngleXU=0 Radius=1
    g238: Circle CenterX=328.643 CenterY=105.865 CenterZ=0 NormalX=0 NormalY=0 NormalZ=1 AngleXU=0 Radius=1
    g239: BSplineCurve PolesCount=3 KnotsCount=2 Degree=2 IsPeriodic=0
    g240: GeomPoint X=336.157 Y=107.779 Z=0
    g241: GeomPoint X=328.643 Y=105.865 Z=0
    g242: LineSegment StartX=322.073 StartY=124.221 StartZ=0 EndX=362.073 EndY=124.221 EndZ=0
    g243: Circle CenterX=371.567 CenterY=-80.8644 CenterZ=0 NormalX=0 NormalY=0 NormalZ=1 AngleXU=0 Radius=1
    g244: Circle CenterX=375.073 CenterY=-82.7896 CenterZ=0 NormalX=0 NormalY=0 NormalZ=1 AngleXU=0 Radius=1
    g245: Circle CenterX=375.073 CenterY=-78.7896 CenterZ=0 NormalX=0 NormalY=0 NormalZ=1 AngleXU=0 Radius=1
    g246: BSplineCurve PolesCount=3 KnotsCount=2 Degree=2 IsPeriodic=0
    g247: GeomPoint X=371.567 Y=-80.8644 Z=0
    g248: GeomPoint X=375.073 Y=-78.7896 Z=0
    g249: Circle CenterX=321.579 CenterY=-53.4075 CenterZ=0 NormalX=0 NormalY=0 NormalZ=1 AngleXU=0 Radius=1
    g250: Circle CenterX=318.073 CenterY=-51.4823 CenterZ=0 NormalX=0 NormalY=0 NormalZ=1 AngleXU=0 Radius=1
    g251: Circle CenterX=318.073 CenterY=-47.4805 CenterZ=0 NormalX=0 NormalY=0 NormalZ=1 AngleXU=0 Radius=1
    g252: BSplineCurve PolesCount=3 KnotsCount=2 Degree=2 IsPeriodic=0
    g253: GeomPoint X=321.579 Y=-53.4075 Z=0
    g254: GeomPoint X=318.073 Y=-47.4805 Z=0
    g255: LineSegment StartX=371.567 StartY=-80.8644 StartZ=0 EndX=321.579 EndY=-53.4075 EndZ=0
    g256: Circle CenterX=321.579 CenterY=-67.3492 CenterZ=0 NormalX=0 NormalY=0 NormalZ=1 AngleXU=0 Radius=1
    g257: Circle CenterX=318.073 CenterY=-65.424 CenterZ=0 NormalX=0 NormalY=0 NormalZ=1 AngleXU=0 Radius=1
    g258: Circle CenterX=318.073 CenterY=-69.424 CenterZ=0 NormalX=0 NormalY=0 NormalZ=1 AngleXU=0 Radius=1
    g259: BSplineCurve PolesCount=3 KnotsCount=2 Degree=2 IsPeriodic=0
    g260: GeomPoint X=321.579 Y=-67.3492 Z=0
    g261: GeomPoint X=318.073 Y=-69.424 Z=0
    g262: Circle CenterX=362.567 CenterY=-89.8542 CenterZ=0 NormalX=0 NormalY=0 NormalZ=1 AngleXU=0 Radius=1
    g263: Circle CenterX=366.073 CenterY=-91.7794 CenterZ=0 NormalX=0 NormalY=0 NormalZ=1 AngleXU=0 Radius=1
    g264: Circle CenterX=362.073 CenterY=-91.7794 CenterZ=0 NormalX=0 NormalY=0 NormalZ=1 AngleXU=0 Radius=1
    g265: BSplineCurve PolesCount=3 KnotsCount=2 Degree=2 IsPeriodic=0
    g266: GeomPoint X=362.567 Y=-89.8542 Z=0
    g267: GeomPoint X=362.073 Y=-91.7794 Z=0
    g268: Circle CenterX=322.073 CenterY=-91.7794 CenterZ=0 NormalX=0 NormalY=0 NormalZ=1 AngleXU=0 Radius=1
    g269: Circle CenterX=318.073 CenterY=-91.7794 CenterZ=0 NormalX=0 NormalY=0 NormalZ=1 AngleXU=0 Radius=1
    g270: Circle CenterX=318.073 CenterY=-87.7794 CenterZ=0 NormalX=0 NormalY=0 NormalZ=1 AngleXU=0 Radius=1
    g271: BSplineCurve PolesCount=3 KnotsCount=2 Degree=2 IsPeriodic=0
    g272: GeomPoint X=322.073 Y=-91.7794 Z=0
    g273: GeomPoint X=318.073 Y=-87.7794 Z=0
    g274: LineSegment StartX=362.567 StartY=-89.8542 StartZ=0 EndX=321.579 EndY=-67.3492 EndZ=0
    g275: LineSegment StartX=318.073 StartY=-69.424 StartZ=0 EndX=318.073 EndY=-87.7794 EndZ=0
    g276: LineSegment StartX=322.073 StartY=-91.7794 StartZ=0 EndX=362.073 EndY=-91.7794 EndZ=0
    g277: Circle CenterX=2.07281 CenterY=124.221 CenterZ=0 NormalX=0 NormalY=0 NormalZ=1 AngleXU=0 Radius=1
    g278: Circle CenterX=1.57905 CenterY=122.295 CenterZ=0 NormalX=0 NormalY=0 NormalZ=1 AngleXU=0 Radius=1
    g279: BSplineCurve PolesCount=3 KnotsCount=2 Degree=2 IsPeriodic=0
    g280: GeomPoint X=2.07281 Y=124.221 Z=0
    g281: GeomPoint X=1.57905 Y=122.295 Z=0
    g282: Circle CenterX=42.0728 CenterY=124.221 CenterZ=0 NormalX=0 NormalY=0 NormalZ=1 AngleXU=0 Radius=1
    g283: Circle CenterX=46.0728 CenterY=124.221 CenterZ=0 NormalX=0 NormalY=0 NormalZ=1 AngleXU=0 Radius=1
    g284: Circle CenterX=46.0728 CenterY=120.221 CenterZ=0 NormalX=0 NormalY=0 NormalZ=1 AngleXU=0 Radius=1
    g285: BSplineCurve PolesCount=3 KnotsCount=2 Degree=2 IsPeriodic=0
    g286: GeomPoint X=42.0728 Y=124.221 Z=0
    g287: GeomPoint X=46.0728 Y=120.221 Z=0
    g288: Circle CenterX=46.0728 CenterY=109.865 CenterZ=0 NormalX=0 NormalY=0 NormalZ=1 AngleXU=0 Radius=1
    g289: Circle CenterX=46.0728 CenterY=105.865 CenterZ=0 NormalX=0 NormalY=0 NormalZ=1 AngleXU=0 Radius=1
    g290: Circle CenterX=42.0728 CenterY=105.865 CenterZ=0 NormalX=0 NormalY=0 NormalZ=1 AngleXU=0 Radius=1
    g291: BSplineCurve PolesCount=3 KnotsCount=2 Degree=2 IsPeriodic=0
    g292: GeomPoint X=46.0728 Y=109.865 Z=0
    g293: GeomPoint X=42.0728 Y=105.865 Z=0
    g294: Circle CenterX=35.5028 CenterY=105.865 CenterZ=0 NormalX=0 NormalY=0 NormalZ=1 AngleXU=0 Radius=1
    g295: Circle CenterX=31.5028 CenterY=105.865 CenterZ=0 NormalX=0 NormalY=0 NormalZ=1 AngleXU=0 Radius=1
    g296: Circle CenterX=27.9965 CenterY=107.79 CenterZ=0 NormalX=0 NormalY=0 NormalZ=1 AngleXU=0 Radius=1
    g297: BSplineCurve PolesCount=3 KnotsCount=2 Degree=2 IsPeriodic=0
    g298: GeomPoint X=35.5028 Y=105.865 Z=0
    g299: GeomPoint X=27.9965 Y=107.79 Z=0
    g300: LineSegment StartX=2.07281 StartY=124.221 StartZ=0 EndX=42.0728 EndY=124.221 EndZ=0
    g301: LineSegment StartX=46.0728 StartY=120.221 StartZ=0 EndX=46.0728 EndY=109.865 EndZ=0
    g302: LineSegment StartX=42.0728 StartY=105.865 StartZ=0 EndX=35.5028 EndY=105.865 EndZ=0
    g303: LineSegment StartX=27.9965 StartY=107.79 StartZ=0 EndX=1.57905 EndY=122.295 EndZ=0
    g304: Circle CenterX=42.5666 CenterY=-67.3492 CenterZ=0 NormalX=0 NormalY=0 NormalZ=1 AngleXU=0 Radius=1
    g305: Circle CenterX=46.0728 CenterY=-65.424 CenterZ=0 NormalX=0 NormalY=0 NormalZ=1 AngleXU=0 Radius=1
    g306: Circle CenterX=46.0728 CenterY=-69.424 CenterZ=0 NormalX=0 NormalY=0 NormalZ=1 AngleXU=0 Radius=1
    g307: BSplineCurve PolesCount=3 KnotsCount=2 Degree=2 IsPeriodic=0
    g308: GeomPoint X=42.5666 Y=-67.3492 Z=0
    g309: GeomPoint X=46.0728 Y=-69.424 Z=0
    g310: Circle CenterX=46.0728 CenterY=-87.7794 CenterZ=0 NormalX=0 NormalY=0 NormalZ=1 AngleXU=0 Radius=1
    g311: Circle CenterX=46.0728 CenterY=-91.7794 CenterZ=0 NormalX=0 NormalY=0 NormalZ=1 AngleXU=0 Radius=1
    g312: Circle CenterX=42.0728 CenterY=-91.7794 CenterZ=0 NormalX=0 NormalY=0 NormalZ=1 AngleXU=0 Radius=1
    g313: BSplineCurve PolesCount=3 KnotsCount=2 Degree=2 IsPeriodic=0
    g314: GeomPoint X=46.0728 Y=-87.7794 Z=0
    g315: GeomPoint X=42.0728 Y=-91.7794 Z=0
    g316: Circle CenterX=2.07281 CenterY=-91.7794 CenterZ=0 NormalX=0 NormalY=0 NormalZ=1 AngleXU=0 Radius=1
    g317: Circle CenterX=-1.92719 CenterY=-91.7794 CenterZ=0 NormalX=0 NormalY=0 NormalZ=1 AngleXU=0 Radius=1
    g318: Circle CenterX=1.57905 CenterY=-89.8542 CenterZ=0 NormalX=0 NormalY=0 NormalZ=1 AngleXU=0 Radius=1
    g319: BSplineCurve PolesCount=3 KnotsCount=2 Degree=2 IsPeriodic=0
    g320: GeomPoint X=2.07281 Y=-91.7794 Z=0
    g321: GeomPoint X=1.57905 Y=-89.8542 Z=0
    g322: LineSegment StartX=2.07281 StartY=-91.7794 StartZ=0 EndX=42.0728 EndY=-91.7794 EndZ=0
    g323: LineSegment StartX=46.0728 StartY=-87.7794 StartZ=0 EndX=46.0728 EndY=-69.424 EndZ=0
    g324: LineSegment StartX=42.5666 StartY=-67.3492 StartZ=0 EndX=1.57905 EndY=-89.8542 EndZ=0
    g325: Circle CenterX=322.073 CenterY=76.4095 CenterZ=0 NormalX=0 NormalY=0 NormalZ=1 AngleXU=0 Radius=4
    g326: BSplineCurve PolesCount=3 KnotsCount=2 Degree=2 IsPeriodic=0
    g327: GeomPoint X=318.073 Y=72.4095 Z=0
    g328: GeomPoint X=322.073 Y=76.4095 Z=0
    g329: Circle CenterX=375.073 CenterY=72.4095 CenterZ=0 NormalX=0 NormalY=0 NormalZ=1 AngleXU=0 Radius=1
    g330: Circle CenterX=375.073 CenterY=76.4095 CenterZ=0 NormalX=0 NormalY=0 NormalZ=1 AngleXU=0 Radius=1
    g331: Circle CenterX=371.073 CenterY=76.4095 CenterZ=0 NormalX=0 NormalY=0 NormalZ=1 AngleXU=0 Radius=1
    g332: BSplineCurve PolesCount=3 KnotsCount=2 Degree=2 IsPeriodic=0
    g333: GeomPoint X=375.073 Y=72.4095 Z=0
    g334: GeomPoint X=371.073 Y=76.4095 Z=0
    g335: LineSegment StartX=322.073 StartY=76.4095 StartZ=0 EndX=371.073 EndY=76.4095 EndZ=0
    g336: LineSegment StartX=318.073 StartY=72.4095 StartZ=0 EndX=318.073 EndY=-47.4805 EndZ=0
    g337: LineSegment StartX=375.073 StartY=72.4095 StartZ=0 EndX=375.073 EndY=-78.7896 EndZ=0
    g338: ArcOfCircle CenterX=-26.9272 CenterY=22.1087 CenterZ=0 NormalX=0 NormalY=0 NormalZ=1 AngleXU=0 Radius=4 StartAngle=5e-16 EndAngle=3.14159
    g339: LineSegment StartX=-22.9272 StartY=22.1087 StartZ=0 EndX=-18.9272 EndY=-83.7794 EndZ=0
    g340: LineSegment StartX=-34.9272 StartY=-83.7794 StartZ=0 EndX=-30.9272 EndY=22.1087 EndZ=0
    g341: ArcOfCircle CenterX=391.073 CenterY=22.1087 CenterZ=0 NormalX=0 NormalY=0 NormalZ=1 AngleXU=0 Radius=4 StartAngle=0 EndAngle=3.14159
    g342: LineSegment StartX=387.073 StartY=22.1087 StartZ=0 EndX=383.073 EndY=-83.7794 EndZ=0
    g343: LineSegment StartX=395.073 StartY=22.1087 StartZ=0 EndX=399.073 EndY=-83.7794 EndZ=0
    g344: Circle CenterX=-10.9272 CenterY=-78.7794 CenterZ=0 NormalX=0 NormalY=0 NormalZ=1 AngleXU=0 Radius=1
    g345: Circle CenterX=-10.9272 CenterY=-82.7794 CenterZ=0 NormalX=0 NormalY=0 NormalZ=1 AngleXU=0 Radius=1
    g346: Circle CenterX=-7.42095 CenterY=-80.8542 CenterZ=0 NormalX=0 NormalY=0 NormalZ=1 AngleXU=0 Radius=1
    g347: BSplineCurve PolesCount=3 KnotsCount=2 Degree=2 IsPeriodic=0
    g348: GeomPoint X=-10.9272 Y=-78.7794 Z=0
    g349: GeomPoint X=-7.42095 Y=-80.8542 Z=0
    g350: Circle CenterX=42.5666 CenterY=-53.4075 CenterZ=0 NormalX=0 NormalY=0 NormalZ=1 AngleXU=0 Radius=1
    g351: Circle CenterX=46.0728 CenterY=-51.4823 CenterZ=0 NormalX=0 NormalY=0 NormalZ=1 AngleXU=0 Radius=1
    g352: Circle CenterX=46.0728 CenterY=-47.4823 CenterZ=0 NormalX=0 NormalY=0 NormalZ=1 AngleXU=0 Radius=1
    g353: BSplineCurve PolesCount=3 KnotsCount=2 Degree=2 IsPeriodic=0
    g354: GeomPoint X=42.5666 Y=-53.4075 Z=0
    g355: GeomPoint X=46.0728 Y=-47.4823 Z=0
    g356: Circle CenterX=46.0728 CenterY=72.4095 CenterZ=0 NormalX=0 NormalY=0 NormalZ=1 AngleXU=0 Radius=1
    g357: Circle CenterX=46.0728 CenterY=76.4095 CenterZ=0 NormalX=0 NormalY=0 NormalZ=1 AngleXU=0 Radius=1
    g358: Circle CenterX=42.0728 CenterY=76.4095 CenterZ=0 NormalX=0 NormalY=0 NormalZ=1 AngleXU=0 Radius=1
    g359: BSplineCurve PolesCount=3 KnotsCount=2 Degree=2 IsPeriodic=0
    g360: GeomPoint X=46.0728 Y=72.4095 Z=0
    g361: GeomPoint X=42.0728 Y=76.4095 Z=0
    g362: Circle CenterX=-6.92718 CenterY=76.4095 CenterZ=0 NormalX=0 NormalY=0 NormalZ=1 AngleXU=0 Radius=1
    g363: Circle CenterX=-10.9272 CenterY=76.4095 CenterZ=0 NormalX=0 NormalY=0 NormalZ=1 AngleXU=0 Radius=1
    g364: Circle CenterX=-10.9272 CenterY=72.4095 CenterZ=0 NormalX=0 NormalY=0 NormalZ=1 AngleXU=0 Radius=1
    g365: BSplineCurve PolesCount=3 KnotsCount=2 Degree=2 IsPeriodic=0
    g366: GeomPoint X=-6.92718 Y=76.4095 Z=0
    g367: GeomPoint X=-10.9272 Y=72.4095 Z=0
    g368: LineSegment StartX=-10.9272 StartY=72.4095 StartZ=0 EndX=-10.9272 EndY=-78.7794 EndZ=0
    g369: LineSegment StartX=-7.42095 StartY=-80.8542 StartZ=0 EndX=42.5666 EndY=-53.4075 EndZ=0
    g370: LineSegment StartX=46.0728 StartY=-47.4823 StartZ=0 EndX=46.0728 EndY=72.4095 EndZ=0
    g371: LineSegment StartX=42.0728 StartY=76.4095 StartZ=0 EndX=-6.92719 EndY=76.4095 EndZ=0
    g372: LineSegment StartX=182.072 StartY=136.221 StartZ=0 EndX=182.072 EndY=137.404 EndZ=0
    g373: LineSegment StartX=182.072 StartY=136.221 StartZ=0 EndX=232.072 EndY=136.221 EndZ=0
    g374: LineSegment StartX=182.072 StartY=136.221 StartZ=0 EndX=132.072 EndY=136.221 EndZ=0
  constraints (618):
    c: Vertical(g0)
    c: Vertical(g1)
    c: Block(g1)
    c: Block(g0)
    c: Weight(g4) = 1
    c: Equal(g4,g5)
    c: Equal(g4,g6)
    c: InternalAlignment(g4,g7)
    c: InternalAlignment(g5,g7)
    c: InternalAlignment(g6,g7)
    c: InternalAlignment(g8,g7)
    c: InternalAlignment(g9,g7)
    c: Weight(g10) = 1
    c: Equal(g10,g11)
    c: Equal(g10,g12)
    c: InternalAlignment(g10,g13)
    c: InternalAlignment(g11,g13)
    c: InternalAlignment(g12,g13)
    c: InternalAlignment(g14,g13)
    c: InternalAlignment(g15,g13)
    c: Block(g13)
    c: Block(g7)
    c: Weight(g16) = 1
    c: Equal(g16,g17)
    c: Equal(g16,g18)
    c: InternalAlignment(g16,g19)
    c: InternalAlignment(g17,g19)
    c: InternalAlignment(g18,g19)
    c: InternalAlignment(g20,g19)
    c: InternalAlignment(g21,g19)
    c: Weight(g22) = 1
    c: Equal(g22,g23)
    c: Equal(g22,g24)
    c: InternalAlignment(g22,g25)
    c: InternalAlignment(g23,g25)
    c: InternalAlignment(g24,g25)
    c: InternalAlignment(g26,g25)
    c: InternalAlignment(g27,g25)
    c: Block(g25)
    c: Block(g19)
    c: Weight(g28) = 1
    c: Equal(g28,g29)
    c: Equal(g28,g30)
    c: InternalAlignment(g28,g31)
    c: InternalAlignment(g29,g31)
    c: InternalAlignment(g30,g31)
    c: InternalAlignment(g32,g31)
    c: InternalAlignment(g33,g31)
    c: Weight(g34) = 1
    c: Equal(g34,g35)
    c: Equal(g34,g36)
    c: InternalAlignment(g34,g37)
    c: InternalAlignment(g35,g37)
    c: InternalAlignment(g36,g37)
    c: InternalAlignment(g38,g37)
    c: InternalAlignment(g39,g37)
    c: Block(g31)
    c: Block(g37)
    c: Coincident(g40,g1)
    c: Coincident(g40,g0)
    c: Horizontal(g40)
    c: Distance(g40) = 450
    c: Weight(g41) = 1
    c: Equal(g41,g42)
    c: Equal(g41,g43)
    c: InternalAlignment(g41,g44)
    c: InternalAlignment(g42,g44)
    c: InternalAlignment(g43,g44)
    c: InternalAlignment(g45,g44)
    c: InternalAlignment(g46,g44)
    c: Block(g44)
    c: Weight(g47) = 1
    c: Equal(g47,g48)
    c: Equal(g47,g49)
    c: InternalAlignment(g47,g50)
    c: InternalAlignment(g48,g50)
    c: InternalAlignment(g49,g50)
    c: InternalAlignment(g51,g50)
    c: InternalAlignment(g52,g50)
    c: Block(g50)
    c: Weight(g53) = 1
    c: Equal(g53,g54)
    c: Equal(g53,g55)
    c: InternalAlignment(g53,g56)
    c: InternalAlignment(g54,g56)
    c: InternalAlignment(g55,g56)
    c: InternalAlignment(g57,g56)
    c: InternalAlignment(g58,g56)
    c: Block(g56)
    c: Weight(g59) = 1
    c: Equal(g59,g60)
    c: Equal(g59,g61)
    c: InternalAlignment(g59,g62)
    c: InternalAlignment(g60,g62)
    c: InternalAlignment(g61,g62)
    c: InternalAlignment(g63,g62)
    c: InternalAlignment(g64,g62)
    c: Block(g62)
    c: Weight(g65) = 1
    c: Equal(g65,g66)
    c: Equal(g65,g67)
    c: InternalAlignment(g65,g68)
    c: InternalAlignment(g66,g68)
    c: InternalAlignment(g67,g68)
    c: InternalAlignment(g69,g68)
    c: InternalAlignment(g70,g68)
    c: Weight(g71) = 1
    c: Equal(g71,g72)
    c: Equal(g71,g73)
    c: InternalAlignment(g71,g74)
    c: InternalAlignment(g72,g74)
    c: InternalAlignment(g73,g74)
    c: InternalAlignment(g75,g74)
    c: InternalAlignment(g76,g74)
    c: Block(g68)
    c: Block(g74)
    c: Coincident(g77,g68)
    c: Coincident(g77,g74)
    c: Vertical(g77)
    c: Coincident(g78,g68)
    c: Coincident(g78,g50)
    c: Coincident(g79,g50)
    c: Coincident(g79,g74)
    c: Weight(g80) = 1
    c: Equal(g80,g81)
    c: Equal(g80,g82)
    c: InternalAlignment(g80,g83)
    c: InternalAlignment(g81,g83)
    c: InternalAlignment(g82,g83)
    c: InternalAlignment(g84,g83)
    c: InternalAlignment(g85,g83)
    c: Weight(g86) = 1
    c: Equal(g86,g87)
    c: Equal(g86,g88)
    c: InternalAlignment(g86,g89)
    c: InternalAlignment(g87,g89)
    c: InternalAlignment(g88,g89)
    c: InternalAlignment(g90,g89)
    c: InternalAlignment(g91,g89)
    c: Block(g83)
    c: Block(g89)
    c: Coincident(g92,g83)
    c: Coincident(g92,g89)
    c: Vertical(g92)
    c: Coincident(g93,g83)
    c: Coincident(g93,g44)
    c: Coincident(g94,g44)
    c: Coincident(g94,g89)
    c: Weight(g95) = 1
    c: Equal(g95,g96)
    c: Equal(g95,g97)
    c: InternalAlignment(g95,g98)
    c: InternalAlignment(g96,g98)
    c: InternalAlignment(g97,g98)
    c: InternalAlignment(g99,g98)
    c: InternalAlignment(g100,g98)
    c: Weight(g101) = 1
    c: Equal(g101,g102)
    c: Equal(g101,g103)
    c: InternalAlignment(g101,g104)
    c: InternalAlignment(g102,g104)
    c: InternalAlignment(g103,g104)
    c: InternalAlignment(g105,g104)
    c: InternalAlignment(g106,g104)
    c: Block(g98)
    c: Block(g104)
    c: Coincident(g107,g98)
    c: Coincident(g107,g104)
    c: Vertical(g107)
    c: Coincident(g108,g104)
    c: Coincident(g108,g62)
    c: Coincident(g109,g62)
    c: Coincident(g109,g98)
    c: Weight(g110) = 1
    c: Equal(g110,g111)
    c: Equal(g110,g112)
    c: InternalAlignment(g110,g113)
    c: InternalAlignment(g111,g113)
    c: InternalAlignment(g112,g113)
    c: InternalAlignment(g114,g113)
    c: InternalAlignment(g115,g113)
    c: Weight(g116) = 1
    c: Equal(g116,g117)
    c: Equal(g116,g118)
    c: InternalAlignment(g116,g119)
    c: InternalAlignment(g117,g119)
    c: InternalAlignment(g118,g119)
    c: InternalAlignment(g120,g119)
    c: InternalAlignment(g121,g119)
    c: Block(g113)
    c: Block(g119)
    c: Coincident(g122,g113)
    c: Coincident(g122,g119)
    c: Vertical(g122)
    c: Coincident(g123,g119)
    c: Coincident(g123,g56)
    c: Coincident(g124,g56)
    c: Coincident(g124,g113)
    c: Weight(g125) = 1
    c: Equal(g125,g126)
    c: Equal(g125,g127)
    c: InternalAlignment(g125,g128)
    c: InternalAlignment(g126,g128)
    c: InternalAlignment(g127,g128)
    c: InternalAlignment(g129,g128)
    c: InternalAlignment(g130,g128)
    c: Weight(g131) = 1
    c: Equal(g131,g132)
    c: Equal(g131,g133)
    c: InternalAlignment(g131,g134)
    c: InternalAlignment(g132,g134)
    c: InternalAlignment(g133,g134)
    c: InternalAlignment(g135,g134)
    c: InternalAlignment(g136,g134)
    c: Weight(g137) = 1
    c: Equal(g137,g138)
    c: Equal(g137,g139)
    c: InternalAlignment(g137,g140)
    c: InternalAlignment(g138,g140)
    c: InternalAlignment(g139,g140)
    c: InternalAlignment(g141,g140)
    c: InternalAlignment(g142,g140)
    c: Weight(g143) = 1
    c: Equal(g143,g144)
    c: Equal(g143,g145)
    c: InternalAlignment(g143,g146)
    c: InternalAlignment(g144,g146)
    c: InternalAlignment(g145,g146)
    c: InternalAlignment(g147,g146)
    c: InternalAlignment(g148,g146)
    c: Block(g146)
    c: Block(g140)
    c: Block(g134)
    c: Block(g128)
    c: Coincident(g149,g25)
    c: Coincident(g149,g146)
    c: Coincident(g150,g146)
    c: Coincident(g150,g140)
    c: Horizontal(g150)
    c: Coincident(g151,g140)
    c: Coincident(g151,g25)
    c: Vertical(g151)
    c: Coincident(g152,g19)
    c: Coincident(g152,g134)
    c: Vertical(g152)
    c: Coincident(g153,g134)
    c: Coincident(g153,g128)
    c: Horizontal(g153)
    c: Coincident(g154,g128)
    c: Coincident(g154,g19)
    c: Weight(g155) = 1
    c: Equal(g155,g156)
    c: Equal(g155,g157)
    c: InternalAlignment(g155,g158)
    c: InternalAlignment(g156,g158)
    c: InternalAlignment(g157,g158)
    c: InternalAlignment(g159,g158)
    c: InternalAlignment(g160,g158)
    c: Weight(g161) = 1
    c: Equal(g161,g162)
    c: Equal(g161,g163)
    c: InternalAlignment(g161,g164)
    c: InternalAlignment(g162,g164)
    c: InternalAlignment(g163,g164)
    c: InternalAlignment(g165,g164)
    c: InternalAlignment(g166,g164)
    c: Weight(g167) = 1
    c: Equal(g167,g168)
    c: Equal(g167,g169)
    c: InternalAlignment(g167,g170)
    c: InternalAlignment(g168,g170)
    c: InternalAlignment(g169,g170)
    c: InternalAlignment(g171,g170)
    c: InternalAlignment(g172,g170)
    c: Weight(g173) = 1
    c: Equal(g173,g174)
    c: Equal(g173,g175)
    c: InternalAlignment(g173,g176)
    c: InternalAlignment(g174,g176)
    c: InternalAlignment(g175,g176)
    c: InternalAlignment(g177,g176)
    c: InternalAlignment(g178,g176)
    c: Block(g176)
    c: Block(g170)
    c: Block(g164)
    c: Block(g158)
    c: Coincident(g179,g176)
    c: Coincident(g179,g170)
    c: Horizontal(g179)
    c: Coincident(g180,g170)
    c: Coincident(g180,g7)
    c: Vertical(g180)
    c: Coincident(g181,g13)
    c: Coincident(g181,g164)
    c: Vertical(g181)
    c: Coincident(g182,g164)
    c: Coincident(g182,g158)
    c: Horizontal(g182)
    c: Coincident(g183,g158)
    c: Coincident(g183,g13)
    c: Coincident(g184,g7)
    c: Weight(g185) = 1
    c: Equal(g185,g186)
    c: Equal(g185,g187)
    c: InternalAlignment(g185,g188)
    c: InternalAlignment(g186,g188)
    c: InternalAlignment(g187,g188)
    c: InternalAlignment(g189,g188)
    c: InternalAlignment(g190,g188)
    c: Weight(g191) = 1
    c: Equal(g191,g192)
    c: Equal(g191,g193)
    c: InternalAlignment(g191,g194)
    c: InternalAlignment(g192,g194)
    c: InternalAlignment(g193,g194)
    c: InternalAlignment(g195,g194)
    c: InternalAlignment(g196,g194)
    c: Block(g194)
    c: Block(g188)
    c: Coincident(g197,g194)
    c: Coincident(g197,g31)
    c: Coincident(g198,g31)
    c: Coincident(g198,g188)
    c: Coincident(g199,g188)
    c: Coincident(g199,g194)
    c: Vertical(g199)
    c: Weight(g200) = 1
    c: Equal(g200,g201)
    c: Equal(g200,g202)
    c: InternalAlignment(g200,g203)
    c: InternalAlignment(g201,g203)
    c: InternalAlignment(g202,g203)
    c: InternalAlignment(g204,g203)
    c: InternalAlignment(g205,g203)
    c: Weight(g206) = 1
    c: Equal(g206,g207)
    c: Equal(g206,g208)
    c: InternalAlignment(g206,g209)
    c: InternalAlignment(g207,g209)
    c: InternalAlignment(g208,g209)
    c: InternalAlignment(g210,g209)
    c: InternalAlignment(g211,g209)
    c: Block(g209)
    c: Block(g203)
    c: Coincident(g212,g203)
    c: Coincident(g212,g37)
    c: Coincident(g213,g37)
    c: Coincident(g213,g209)
    c: Coincident(g214,g209)
    c: Coincident(g214,g203)
    c: Vertical(g214)
    c: Horizontal(g215)
    c: Block(g215)
    c: Vertical(g216)
    c: Block(g216)
    c: Block(g217)
    c: Weight(g218) = 1
    c: Equal(g218,g219)
    c: Equal(g218,g220)
    c: InternalAlignment(g218,g221)
    c: InternalAlignment(g219,g221)
    c: InternalAlignment(g220,g221)
    c: InternalAlignment(g222,g221)
    c: InternalAlignment(g223,g221)
    c: Weight(g224) = 1
    c: Equal(g224,g225)
    c: Equal(g224,g226)
    c: InternalAlignment(g224,g227)
    c: InternalAlignment(g225,g227)
    c: InternalAlignment(g226,g227)
    c: InternalAlignment(g228,g227)
    c: InternalAlignment(g229,g227)
    c: Weight(g230) = 1
    c: Equal(g230,g231)
    c: Equal(g230,g232)
    c: InternalAlignment(g230,g233)
    c: InternalAlignment(g231,g233)
    c: InternalAlignment(g232,g233)
    c: InternalAlignment(g234,g233)
    c: InternalAlignment(g235,g233)
    c: Weight(g236) = 1
    c: Equal(g236,g237)
    c: Equal(g236,g238)
    c: InternalAlignment(g236,g239)
    c: InternalAlignment(g237,g239)
    c: InternalAlignment(g238,g239)
    c: InternalAlignment(g240,g239)
    c: InternalAlignment(g241,g239)
    c: Block(g221)
    c: Block(g227)
    c: Block(g233)
    c: Block(g239)
    c: Coincident(g242,g227)
    c: Coincident(g242,g221)
    c: Horizontal(g242)
    c: Block(g184)
    c: Weight(g243) = 1
    c: Equal(g243,g244)
    c: Equal(g243,g245)
    c: InternalAlignment(g243,g246)
    c: InternalAlignment(g244,g246)
    c: InternalAlignment(g245,g246)
    c: InternalAlignment(g247,g246)
    c: InternalAlignment(g248,g246)
    c: Weight(g249) = 1
    c: Equal(g249,g250)
    c: Equal(g249,g251)
    c: InternalAlignment(g249,g252)
    c: InternalAlignment(g250,g252)
    c: InternalAlignment(g251,g252)
    c: InternalAlignment(g253,g252)
    c: InternalAlignment(g254,g252)
    c: Block(g246)
    c: Block(g252)
    c: Coincident(g255,g246)
    c: Coincident(g255,g252)
    c: Weight(g256) = 1
    c: Equal(g256,g257)
    c: Equal(g256,g258)
    c: InternalAlignment(g256,g259)
    c: InternalAlignment(g257,g259)
    c: InternalAlignment(g258,g259)
    c: InternalAlignment(g260,g259)
    c: InternalAlignment(g261,g259)
    c: Weight(g262) = 1
    c: Equal(g262,g263)
    c: Equal(g262,g264)
    c: InternalAlignment(g262,g265)
    c: InternalAlignment(g263,g265)
    c: InternalAlignment(g264,g265)
    c: InternalAlignment(g266,g265)
    c: InternalAlignment(g267,g265)
    c: Weight(g268) = 1
    c: Equal(g268,g269)
    c: Equal(g268,g270)
    c: InternalAlignment(g268,g271)
    c: InternalAlignment(g269,g271)
    c: InternalAlignment(g270,g271)
    c: InternalAlignment(g272,g271)
    c: InternalAlignment(g273,g271)
    c: Block(g271)
    c: Block(g265)
    c: Block(g259)
    c: Coincident(g274,g265)
    c: Coincident(g274,g259)
    c: Coincident(g275,g259)
    c: Coincident(g275,g271)
    c: Vertical(g275)
    c: Coincident(g276,g271)
    c: Coincident(g276,g265)
    c: Horizontal(g276)
    c: Weight(g277) = 1
    c: Equal(g277,g278)
    c: InternalAlignment(g277,g279)
    c: InternalAlignment(g278,g279)
    c: InternalAlignment(g280,g279)
    c: InternalAlignment(g281,g279)
    c: Weight(g282) = 1
    c: InternalAlignment(g283,g285)
    c: InternalAlignment(g284,g285)
    c: InternalAlignment(g286,g285)
    c: InternalAlignment(g287,g285)
    c: Weight(g288) = 1
    c: Equal(g288,g289)
    c: Equal(g288,g290)
    c: InternalAlignment(g288,g291)
    c: InternalAlignment(g289,g291)
    c: InternalAlignment(g290,g291)
    c: InternalAlignment(g292,g291)
    c: InternalAlignment(g293,g291)
    c: Equal(g294,g295)
    c: Equal(g294,g296)
    c: InternalAlignment(g294,g297)
    c: InternalAlignment(g295,g297)
    c: InternalAlignment(g296,g297)
    c: InternalAlignment(g298,g297)
    c: InternalAlignment(g299,g297)
    c: Block(g285)
    c: Block(g291)
    c: Block(g297)
    c: Block(g279)
    c: Coincident(g300,g279)
    c: Coincident(g300,g285)
    c: Horizontal(g300)
    c: Coincident(g301,g285)
    c: Coincident(g301,g291)
    c: Vertical(g301)
    c: Coincident(g302,g291)
    c: Coincident(g302,g297)
    c: Horizontal(g302)
    c: Coincident(g303,g297)
    c: Coincident(g303,g279)
    c: Weight(g304) = 1
    c: Equal(g304,g305)
    c: Equal(g304,g306)
    c: InternalAlignment(g304,g307)
    c: InternalAlignment(g305,g307)
    c: InternalAlignment(g306,g307)
    c: InternalAlignment(g308,g307)
    c: InternalAlignment(g309,g307)
    c: Weight(g310) = 1
    c: Equal(g310,g311)
    c: Equal(g310,g312)
    c: InternalAlignment(g310,g313)
    c: InternalAlignment(g311,g313)
    c: InternalAlignment(g312,g313)
    c: InternalAlignment(g314,g313)
    c: InternalAlignment(g315,g313)
    c: Weight(g316) = 1
    c: Equal(g316,g317)
    c: Equal(g316,g318)
    c: InternalAlignment(g316,g319)
    c: InternalAlignment(g317,g319)
    c: InternalAlignment(g318,g319)
    c: InternalAlignment(g320,g319)
    c: InternalAlignment(g321,g319)
    c: Block(g319)
    c: Block(g313)
    c: Block(g307)
    c: Coincident(g322,g319)
    c: Coincident(g322,g313)
    c: Horizontal(g322)
    c: Coincident(g323,g313)
    c: Coincident(g323,g307)
    c: Vertical(g323)
    c: Coincident(g324,g307)
    c: Coincident(g324,g319)
    c: InternalAlignment(g325,g326)
    c: InternalAlignment(g327,g326)
    c: InternalAlignment(g328,g326)
    c: Block(g326)
    c: Equal(g329,g330)
    c: Equal(g329,g331)
    c: InternalAlignment(g329,g332)
    c: InternalAlignment(g330,g332)
    c: InternalAlignment(g331,g332)
    c: InternalAlignment(g333,g332)
    c: InternalAlignment(g334,g332)
    c: Block(g332)
    c: Coincident(g335,g326)
    c: Horizontal(g335)
    c: Block(g335)
    c: Coincident(g336,g326)
    c: Coincident(g336,g252)
    c: Vertical(g336)
    c: Coincident(g337,g332)
    c: Coincident(g337,g246)
    c: Vertical(g337)
    c: Block(g338)
    c: Block(g2)
    c: Distance(g336) = 119.89
    c: Coincident(g339,g338)
    c: Coincident(g339,g2)
    c: Coincident(g340,g2)
    c: Coincident(g340,g338)
    c: Block(g3)
    c: Block(g341)
    c: Coincident(g342,g341)
    c: Coincident(g342,g3)
    c: Coincident(g343,g341)
    c: Coincident(g343,g3)
    c: Block(g343)
    c: Block(g342)
    c: Weight(g344) = 1
    c: Equal(g344,g345)
    c: Equal(g344,g346)
    c: InternalAlignment(g344,g347)
    c: InternalAlignment(g345,g347)
    c: InternalAlignment(g346,g347)
    c: InternalAlignment(g348,g347)
    c: InternalAlignment(g349,g347)
    c: Weight(g350) = 1
    c: Equal(g350,g351)
    c: Equal(g350,g352)
    c: InternalAlignment(g350,g353)
    c: InternalAlignment(g351,g353)
    c: InternalAlignment(g352,g353)
    c: InternalAlignment(g354,g353)
    c: InternalAlignment(g355,g353)
    c: Weight(g356) = 1
    c: Equal(g356,g357)
    c: Equal(g356,g358)
    c: InternalAlignment(g356,g359)
    c: InternalAlignment(g357,g359)
    c: InternalAlignment(g358,g359)
    c: InternalAlignment(g360,g359)
    c: InternalAlignment(g361,g359)
    c: Weight(g362) = 1
    c: Equal(g362,g363)
    c: Equal(g362,g364)
    c: InternalAlignment(g362,g365)
    c: InternalAlignment(g363,g365)
    c: InternalAlignment(g364,g365)
    c: InternalAlignment(g366,g365)
    c: InternalAlignment(g367,g365)
    c: Block(g365)
    c: Block(g359)
    c: Block(g353)
    c: Block(g347)
    c: Coincident(g368,g365)
    c: Coincident(g368,g347)
    c: Vertical(g368)
    c: Coincident(g369,g347)
    c: Coincident(g369,g353)
    c: Coincident(g370,g353)
    c: Coincident(g370,g359)
    c: Vertical(g370)
    c: Coincident(g371,g359)
    c: Coincident(g371,g365)
    c: Horizontal(g371)
    c: Vertical(g372)
    c: Block(g372)
    c: Coincident(g373,g372)
    c: Horizontal(g373)
    c: Distance(g373) = 50
    c: Coincident(g374,g372)
    c: Horizontal(g374)
    c: Distance(g374) = 50
FEATURE [Part::Extrusion] Extrude005
  Base = -> Sketch003
  Dir = (0,0,1)
  DirMode = 2
  FaceMakerClass = Part::FaceMakerBullseye
  LengthFwd = 24
  LengthRev = 0
  Solid = true
  Symmetric = false
